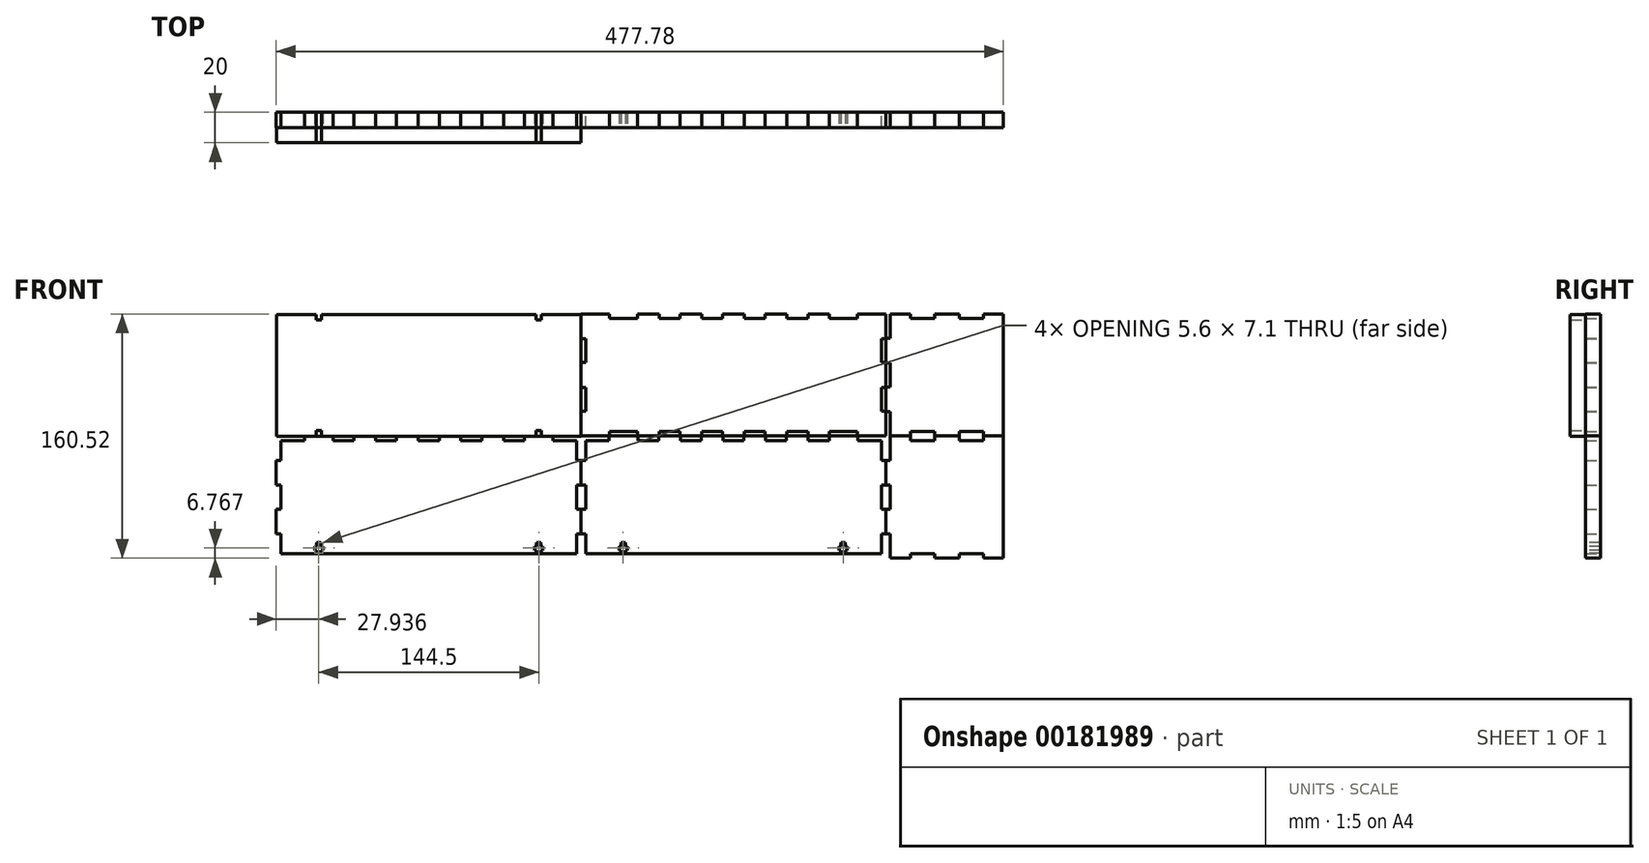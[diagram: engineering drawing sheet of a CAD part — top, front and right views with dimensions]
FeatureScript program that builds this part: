
annotation { "Feature Type Name" : "Feature", "Feature Type Description" : "" }
export const myFeature = defineFeature(function(context is Context, id is Id, definition is map)
    precondition{}
    {
        {
            var Q0;
            Q0=qCreatedBy(makeId("Front.planeOp"),FACE);
            var sketch = newSketch(context, id + "F0", { "sketchPlane" : qUnion([Q0])});
            skLineSegment(sketch, "E0", {"start": v(-38.63, 80.26) * mm, "end": v(-19.87, 80.26) * mm});
            skLineSegment(sketch, "E1", {"start": v(-19.87, 80.26) * mm, "end": v(-19.87, 77.26) * mm});
            skLineSegment(sketch, "E2", {"start": v(-19.87, 77.26) * mm, "end": v(-1.63, 77.26) * mm});
            skLineSegment(sketch, "E3", {"start": v(-1.63, 77.26) * mm, "end": v(-1.63, 80.26) * mm});
            skLineSegment(sketch, "E4", {"start": v(-1.63, 80.26) * mm, "end": v(12.63, 80.26) * mm});
            skLineSegment(sketch, "E5", {"start": v(12.63, 80.26) * mm, "end": v(12.63, 77.26) * mm});
            skLineSegment(sketch, "E6", {"start": v(12.63, 77.26) * mm, "end": v(26.37, 77.26) * mm});
            skLineSegment(sketch, "E7", {"start": v(26.37, 77.26) * mm, "end": v(26.37, 80.26) * mm});
            skLineSegment(sketch, "E8", {"start": v(26.37, 80.26) * mm, "end": v(40.63, 80.26) * mm});
            skLineSegment(sketch, "E9", {"start": v(40.63, 80.26) * mm, "end": v(40.63, 77.26) * mm});
            skLineSegment(sketch, "E10", {"start": v(40.63, 77.26) * mm, "end": v(54.37, 77.26) * mm});
            skLineSegment(sketch, "E11", {"start": v(54.37, 77.26) * mm, "end": v(54.37, 80.26) * mm});
            skLineSegment(sketch, "E12", {"start": v(54.37, 80.26) * mm, "end": v(68.63, 80.26) * mm});
            skLineSegment(sketch, "E13", {"start": v(68.63, 80.26) * mm, "end": v(68.63, 77.26) * mm});
            skLineSegment(sketch, "E14", {"start": v(68.63, 77.26) * mm, "end": v(82.37, 77.26) * mm});
            skLineSegment(sketch, "E15", {"start": v(82.37, 77.26) * mm, "end": v(82.37, 80.26) * mm});
            skLineSegment(sketch, "E16", {"start": v(82.37, 80.26) * mm, "end": v(96.63, 80.26) * mm});
            skLineSegment(sketch, "E17", {"start": v(96.63, 80.26) * mm, "end": v(96.63, 77.26) * mm});
            skLineSegment(sketch, "E18", {"start": v(96.63, 77.26) * mm, "end": v(110.37, 77.26) * mm});
            skLineSegment(sketch, "E19", {"start": v(110.37, 77.26) * mm, "end": v(110.37, 80.26) * mm});
            skLineSegment(sketch, "E20", {"start": v(110.37, 80.26) * mm, "end": v(124.63, 80.26) * mm});
            skLineSegment(sketch, "E21", {"start": v(124.63, 80.26) * mm, "end": v(124.63, 77.26) * mm});
            skLineSegment(sketch, "E22", {"start": v(124.63, 77.26) * mm, "end": v(142.87, 77.26) * mm});
            skLineSegment(sketch, "E23", {"start": v(142.87, 77.26) * mm, "end": v(142.87, 80.26) * mm});
            skLineSegment(sketch, "E24", {"start": v(142.87, 80.26) * mm, "end": v(161.63, 80.26) * mm});
            skLineSegment(sketch, "E25", {"start": v(161.63, 80.26) * mm, "end": v(161.63, 64) * mm});
            skLineSegment(sketch, "E26", {"start": v(161.63, 64) * mm, "end": v(158.63, 64) * mm});
            skLineSegment(sketch, "E27", {"start": v(158.63, 64) * mm, "end": v(158.63, 48.26) * mm});
            skLineSegment(sketch, "E28", {"start": v(158.63, 48.26) * mm, "end": v(161.63, 48.26) * mm});
            skLineSegment(sketch, "E29", {"start": v(161.63, 48.26) * mm, "end": v(161.63, 32) * mm});
            skLineSegment(sketch, "E30", {"start": v(161.63, 32) * mm, "end": v(158.63, 32) * mm});
            skLineSegment(sketch, "E31", {"start": v(158.63, 32) * mm, "end": v(158.63, 16.26) * mm});
            skLineSegment(sketch, "E32", {"start": v(158.63, 16.26) * mm, "end": v(161.63, 16.26) * mm});
            skLineSegment(sketch, "E33", {"start": v(161.63, 16.26) * mm, "end": v(161.63, 0) * mm});
            skLineSegment(sketch, "E34", {"start": v(161.63, 0) * mm, "end": v(142.87, 0) * mm});
            skLineSegment(sketch, "E35", {"start": v(142.87, 0) * mm, "end": v(142.87, 3) * mm});
            skLineSegment(sketch, "E36", {"start": v(142.87, 3) * mm, "end": v(124.63, 3) * mm});
            skLineSegment(sketch, "E37", {"start": v(124.63, 3) * mm, "end": v(124.63, 0) * mm});
            skLineSegment(sketch, "E38", {"start": v(124.63, 0) * mm, "end": v(110.37, 0) * mm});
            skLineSegment(sketch, "E39", {"start": v(110.37, 0) * mm, "end": v(110.37, 3) * mm});
            skLineSegment(sketch, "E40", {"start": v(110.37, 3) * mm, "end": v(96.63, 3) * mm});
            skLineSegment(sketch, "E41", {"start": v(96.63, 3) * mm, "end": v(96.63, 0) * mm});
            skLineSegment(sketch, "E42", {"start": v(96.63, 0) * mm, "end": v(82.37, 0) * mm});
            skLineSegment(sketch, "E43", {"start": v(82.37, 0) * mm, "end": v(82.37, 3) * mm});
            skLineSegment(sketch, "E44", {"start": v(82.37, 3) * mm, "end": v(68.63, 3) * mm});
            skLineSegment(sketch, "E45", {"start": v(68.63, 3) * mm, "end": v(68.63, 0) * mm});
            skLineSegment(sketch, "E46", {"start": v(68.63, 0) * mm, "end": v(54.37, 0) * mm});
            skLineSegment(sketch, "E47", {"start": v(54.37, 0) * mm, "end": v(54.37, 3) * mm});
            skLineSegment(sketch, "E48", {"start": v(54.37, 3) * mm, "end": v(40.63, 3) * mm});
            skLineSegment(sketch, "E49", {"start": v(40.63, 3) * mm, "end": v(40.63, 0) * mm});
            skLineSegment(sketch, "E50", {"start": v(40.63, 0) * mm, "end": v(26.37, 0) * mm});
            skLineSegment(sketch, "E51", {"start": v(26.37, 0) * mm, "end": v(26.37, 3) * mm});
            skLineSegment(sketch, "E52", {"start": v(26.37, 3) * mm, "end": v(12.63, 3) * mm});
            skLineSegment(sketch, "E53", {"start": v(12.63, 3) * mm, "end": v(12.63, 0) * mm});
            skLineSegment(sketch, "E54", {"start": v(12.63, 0) * mm, "end": v(-1.63, 0) * mm});
            skLineSegment(sketch, "E55", {"start": v(-1.63, 0) * mm, "end": v(-1.63, 3) * mm});
            skLineSegment(sketch, "E56", {"start": v(-1.63, 3) * mm, "end": v(-19.87, 3) * mm});
            skLineSegment(sketch, "E57", {"start": v(-19.87, 3) * mm, "end": v(-19.87, 0) * mm});
            skLineSegment(sketch, "E58", {"start": v(-19.87, 0) * mm, "end": v(-38.63, 0) * mm});
            skLineSegment(sketch, "E59", {"start": v(-38.63, 0) * mm, "end": v(-38.63, 16.26) * mm});
            skLineSegment(sketch, "E60", {"start": v(-38.63, 16.26) * mm, "end": v(-35.63, 16.26) * mm});
            skLineSegment(sketch, "E61", {"start": v(-35.63, 16.26) * mm, "end": v(-35.63, 32) * mm});
            skLineSegment(sketch, "E62", {"start": v(-35.63, 32) * mm, "end": v(-38.63, 32) * mm});
            skLineSegment(sketch, "E63", {"start": v(-38.63, 32) * mm, "end": v(-38.63, 48.26) * mm});
            skLineSegment(sketch, "E64", {"start": v(-38.63, 48.26) * mm, "end": v(-35.63, 48.26) * mm});
            skLineSegment(sketch, "E65", {"start": v(-35.63, 48.26) * mm, "end": v(-35.63, 64) * mm});
            skLineSegment(sketch, "E66", {"start": v(-35.63, 64) * mm, "end": v(-38.63, 64) * mm});
            skLineSegment(sketch, "E67", {"start": v(-38.63, 64) * mm, "end": v(-38.63, 80.26) * mm});
            skLineSegment(sketch, "E68", {"start": v(238.89, 0) * mm, "end": v(225.63, 0) * mm});
            skLineSegment(sketch, "E69", {"start": v(225.63, 0) * mm, "end": v(225.63, 3) * mm});
            skLineSegment(sketch, "E70", {"start": v(225.63, 3) * mm, "end": v(209.89, 3) * mm});
            skLineSegment(sketch, "E71", {"start": v(209.89, 3) * mm, "end": v(209.89, 0) * mm});
            skLineSegment(sketch, "E72", {"start": v(209.89, 0) * mm, "end": v(193.63, 0) * mm});
            skLineSegment(sketch, "E73", {"start": v(193.63, 0) * mm, "end": v(193.63, 3) * mm});
            skLineSegment(sketch, "E74", {"start": v(193.63, 3) * mm, "end": v(177.89, 3) * mm});
            skLineSegment(sketch, "E75", {"start": v(177.89, 3) * mm, "end": v(177.89, 0) * mm});
            skLineSegment(sketch, "E76", {"start": v(177.89, 0) * mm, "end": v(164.63, 0) * mm});
            skLineSegment(sketch, "E77", {"start": v(164.63, 0) * mm, "end": v(164.63, 16) * mm});
            skLineSegment(sketch, "E78", {"start": v(164.63, 16) * mm, "end": v(161.63, 16) * mm});
            skLineSegment(sketch, "E79", {"start": v(161.63, 16) * mm, "end": v(161.63, 32.26) * mm});
            skLineSegment(sketch, "E80", {"start": v(161.63, 32.26) * mm, "end": v(164.63, 32.26) * mm});
            skLineSegment(sketch, "E81", {"start": v(164.63, 32.26) * mm, "end": v(164.63, 48) * mm});
            skLineSegment(sketch, "E82", {"start": v(164.63, 48) * mm, "end": v(161.63, 48) * mm});
            skLineSegment(sketch, "E83", {"start": v(161.63, 48) * mm, "end": v(161.63, 64.26) * mm});
            skLineSegment(sketch, "E84", {"start": v(161.63, 64.26) * mm, "end": v(164.63, 64.26) * mm});
            skLineSegment(sketch, "E85", {"start": v(164.63, 64.26) * mm, "end": v(164.63, 80.26) * mm});
            skLineSegment(sketch, "E86", {"start": v(164.63, 80.26) * mm, "end": v(177.89, 80.26) * mm});
            skLineSegment(sketch, "E87", {"start": v(177.89, 80.26) * mm, "end": v(177.89, 77.26) * mm});
            skLineSegment(sketch, "E88", {"start": v(177.89, 77.26) * mm, "end": v(193.63, 77.26) * mm});
            skLineSegment(sketch, "E89", {"start": v(193.63, 77.26) * mm, "end": v(193.63, 80.26) * mm});
            skLineSegment(sketch, "E90", {"start": v(193.63, 80.26) * mm, "end": v(209.89, 80.26) * mm});
            skLineSegment(sketch, "E91", {"start": v(209.89, 80.26) * mm, "end": v(209.89, 77.26) * mm});
            skLineSegment(sketch, "E92", {"start": v(209.89, 77.26) * mm, "end": v(225.63, 77.26) * mm});
            skLineSegment(sketch, "E93", {"start": v(225.63, 77.26) * mm, "end": v(225.63, 80.26) * mm});
            skLineSegment(sketch, "E94", {"start": v(225.63, 80.26) * mm, "end": v(238.89, 80.26) * mm});
            skLineSegment(sketch, "E95", {"start": v(238.89, -80.26) * mm, "end": v(225.63, -80.26) * mm});
            skLineSegment(sketch, "E96", {"start": v(225.63, -80.26) * mm, "end": v(225.63, -77.26) * mm});
            skLineSegment(sketch, "E97", {"start": v(225.63, -77.26) * mm, "end": v(209.89, -77.26) * mm});
            skLineSegment(sketch, "E98", {"start": v(209.89, -77.26) * mm, "end": v(209.89, -80.26) * mm});
            skLineSegment(sketch, "E99", {"start": v(209.89, -80.26) * mm, "end": v(193.63, -80.26) * mm});
            skLineSegment(sketch, "E100", {"start": v(193.63, -80.26) * mm, "end": v(193.63, -77.26) * mm});
            skLineSegment(sketch, "E101", {"start": v(193.63, -77.26) * mm, "end": v(177.89, -77.26) * mm});
            skLineSegment(sketch, "E102", {"start": v(177.89, -77.26) * mm, "end": v(177.89, -80.26) * mm});
            skLineSegment(sketch, "E103", {"start": v(177.89, -80.26) * mm, "end": v(164.63, -80.26) * mm});
            skLineSegment(sketch, "E104", {"start": v(164.63, -80.26) * mm, "end": v(164.63, -64.26) * mm});
            skLineSegment(sketch, "E105", {"start": v(164.63, -64.26) * mm, "end": v(161.63, -64.26) * mm});
            skLineSegment(sketch, "E106", {"start": v(161.63, -64.26) * mm, "end": v(161.63, -48) * mm});
            skLineSegment(sketch, "E107", {"start": v(161.63, -48) * mm, "end": v(164.63, -48) * mm});
            skLineSegment(sketch, "E108", {"start": v(164.63, -48) * mm, "end": v(164.63, -32.26) * mm});
            skLineSegment(sketch, "E109", {"start": v(164.63, -32.26) * mm, "end": v(161.63, -32.26) * mm});
            skLineSegment(sketch, "E110", {"start": v(161.63, -32.26) * mm, "end": v(161.63, -16) * mm});
            skLineSegment(sketch, "E111", {"start": v(161.63, -16) * mm, "end": v(164.63, -16) * mm});
            skLineSegment(sketch, "E112", {"start": v(164.63, -16) * mm, "end": v(164.63, 0) * mm});
            skLineSegment(sketch, "E113", {"start": v(164.63, 0) * mm, "end": v(177.89, 0) * mm});
            skLineSegment(sketch, "E114", {"start": v(177.89, 0) * mm, "end": v(177.89, -3) * mm});
            skLineSegment(sketch, "E115", {"start": v(177.89, -3) * mm, "end": v(193.63, -3) * mm});
            skLineSegment(sketch, "E116", {"start": v(193.63, -3) * mm, "end": v(193.63, 0) * mm});
            skLineSegment(sketch, "E117", {"start": v(193.63, 0) * mm, "end": v(209.89, 0) * mm});
            skLineSegment(sketch, "E118", {"start": v(209.89, 0) * mm, "end": v(209.89, -3) * mm});
            skLineSegment(sketch, "E119", {"start": v(209.89, -3) * mm, "end": v(225.63, -3) * mm});
            skLineSegment(sketch, "E120", {"start": v(225.63, -3) * mm, "end": v(225.63, 0) * mm});
            skLineSegment(sketch, "E121", {"start": v(225.63, 0) * mm, "end": v(238.89, 0) * mm});
            skLineSegment(sketch, "E122", {"start": v(-235.89, -77.26) * mm, "end": v(-235.89, -64.26) * mm});
            skLineSegment(sketch, "E123", {"start": v(-235.89, -64.26) * mm, "end": v(-238.89, -64.26) * mm});
            skLineSegment(sketch, "E124", {"start": v(-238.89, -64.26) * mm, "end": v(-238.89, -48) * mm});
            skLineSegment(sketch, "E125", {"start": v(-238.89, -48) * mm, "end": v(-235.89, -48) * mm});
            skLineSegment(sketch, "E126", {"start": v(-235.89, -48) * mm, "end": v(-235.89, -32.26) * mm});
            skLineSegment(sketch, "E127", {"start": v(-235.89, -32.26) * mm, "end": v(-238.89, -32.26) * mm});
            skLineSegment(sketch, "E128", {"start": v(-238.89, -32.26) * mm, "end": v(-238.89, -16) * mm});
            skLineSegment(sketch, "E129", {"start": v(-238.89, -16) * mm, "end": v(-235.89, -16) * mm});
            skLineSegment(sketch, "E130", {"start": v(-235.89, -16) * mm, "end": v(-235.89, -3) * mm});
            skLineSegment(sketch, "E131", {"start": v(-235.89, -3) * mm, "end": v(-220.39, -3) * mm});
            skLineSegment(sketch, "E132", {"start": v(-220.39, -3) * mm, "end": v(-220.39, 0) * mm});
            skLineSegment(sketch, "E133", {"start": v(-220.39, 0) * mm, "end": v(-201.63, 0) * mm});
            skLineSegment(sketch, "E134", {"start": v(-201.63, 0) * mm, "end": v(-201.63, -3) * mm});
            skLineSegment(sketch, "E135", {"start": v(-201.63, -3) * mm, "end": v(-187.89, -3) * mm});
            skLineSegment(sketch, "E136", {"start": v(-187.89, -3) * mm, "end": v(-187.89, 0) * mm});
            skLineSegment(sketch, "E137", {"start": v(-187.89, 0) * mm, "end": v(-173.63, 0) * mm});
            skLineSegment(sketch, "E138", {"start": v(-173.63, 0) * mm, "end": v(-173.63, -3) * mm});
            skLineSegment(sketch, "E139", {"start": v(-173.63, -3) * mm, "end": v(-159.89, -3) * mm});
            skLineSegment(sketch, "E140", {"start": v(-159.89, -3) * mm, "end": v(-159.89, 0) * mm});
            skLineSegment(sketch, "E141", {"start": v(-159.89, 0) * mm, "end": v(-145.63, 0) * mm});
            skLineSegment(sketch, "E142", {"start": v(-145.63, 0) * mm, "end": v(-145.63, -3) * mm});
            skLineSegment(sketch, "E143", {"start": v(-145.63, -3) * mm, "end": v(-131.89, -3) * mm});
            skLineSegment(sketch, "E144", {"start": v(-131.89, -3) * mm, "end": v(-131.89, 0) * mm});
            skLineSegment(sketch, "E145", {"start": v(-131.89, 0) * mm, "end": v(-117.63, 0) * mm});
            skLineSegment(sketch, "E146", {"start": v(-117.63, 0) * mm, "end": v(-117.63, -3) * mm});
            skLineSegment(sketch, "E147", {"start": v(-117.63, -3) * mm, "end": v(-103.89, -3) * mm});
            skLineSegment(sketch, "E148", {"start": v(-103.89, -3) * mm, "end": v(-103.89, 0) * mm});
            skLineSegment(sketch, "E149", {"start": v(-103.89, 0) * mm, "end": v(-89.63, 0) * mm});
            skLineSegment(sketch, "E150", {"start": v(-89.63, 0) * mm, "end": v(-89.63, -3) * mm});
            skLineSegment(sketch, "E151", {"start": v(-89.63, -3) * mm, "end": v(-75.89, -3) * mm});
            skLineSegment(sketch, "E152", {"start": v(-75.89, -3) * mm, "end": v(-75.89, 0) * mm});
            skLineSegment(sketch, "E153", {"start": v(-75.89, 0) * mm, "end": v(-57.13, 0) * mm});
            skLineSegment(sketch, "E154", {"start": v(-57.13, 0) * mm, "end": v(-57.13, -3) * mm});
            skLineSegment(sketch, "E155", {"start": v(-57.13, -3) * mm, "end": v(-41.63, -3) * mm});
            skLineSegment(sketch, "E156", {"start": v(-41.63, -3) * mm, "end": v(-41.63, -16) * mm});
            skLineSegment(sketch, "E157", {"start": v(-41.63, -16) * mm, "end": v(-38.63, -16) * mm});
            skLineSegment(sketch, "E158", {"start": v(-38.63, -16) * mm, "end": v(-38.63, -32.26) * mm});
            skLineSegment(sketch, "E159", {"start": v(-38.63, -32.26) * mm, "end": v(-41.63, -32.26) * mm});
            skLineSegment(sketch, "E160", {"start": v(-41.63, -32.26) * mm, "end": v(-41.63, -48) * mm});
            skLineSegment(sketch, "E161", {"start": v(-41.63, -48) * mm, "end": v(-38.63, -48) * mm});
            skLineSegment(sketch, "E162", {"start": v(-38.63, -48) * mm, "end": v(-38.63, -64.26) * mm});
            skLineSegment(sketch, "E163", {"start": v(-38.63, -64.26) * mm, "end": v(-41.63, -64.26) * mm});
            skLineSegment(sketch, "E164", {"start": v(-41.63, -64.26) * mm, "end": v(-41.63, -77.26) * mm});
            skLineSegment(sketch, "E165", {"start": v(-35.63, -77.26) * mm, "end": v(-35.63, -64.26) * mm});
            skLineSegment(sketch, "E166", {"start": v(-35.63, -64.26) * mm, "end": v(-38.63, -64.26) * mm});
            skLineSegment(sketch, "E167", {"start": v(-38.63, -64.26) * mm, "end": v(-38.63, -48) * mm});
            skLineSegment(sketch, "E168", {"start": v(-38.63, -48) * mm, "end": v(-35.63, -48) * mm});
            skLineSegment(sketch, "E169", {"start": v(-35.63, -48) * mm, "end": v(-35.63, -32.26) * mm});
            skLineSegment(sketch, "E170", {"start": v(-35.63, -32.26) * mm, "end": v(-38.63, -32.26) * mm});
            skLineSegment(sketch, "E171", {"start": v(-38.63, -32.26) * mm, "end": v(-38.63, -16) * mm});
            skLineSegment(sketch, "E172", {"start": v(-38.63, -16) * mm, "end": v(-35.63, -16) * mm});
            skLineSegment(sketch, "E173", {"start": v(-35.63, -16) * mm, "end": v(-35.63, -3) * mm});
            skLineSegment(sketch, "E174", {"start": v(-35.63, -3) * mm, "end": v(-20.13, -3) * mm});
            skLineSegment(sketch, "E175", {"start": v(-20.13, -3) * mm, "end": v(-20.13, 0) * mm});
            skLineSegment(sketch, "E176", {"start": v(-20.13, 0) * mm, "end": v(-1.37, 0) * mm});
            skLineSegment(sketch, "E177", {"start": v(-1.37, 0) * mm, "end": v(-1.37, -3) * mm});
            skLineSegment(sketch, "E178", {"start": v(-1.37, -3) * mm, "end": v(12.37, -3) * mm});
            skLineSegment(sketch, "E179", {"start": v(12.37, -3) * mm, "end": v(12.37, 0) * mm});
            skLineSegment(sketch, "E180", {"start": v(12.37, 0) * mm, "end": v(26.63, 0) * mm});
            skLineSegment(sketch, "E181", {"start": v(26.63, 0) * mm, "end": v(26.63, -3) * mm});
            skLineSegment(sketch, "E182", {"start": v(26.63, -3) * mm, "end": v(40.37, -3) * mm});
            skLineSegment(sketch, "E183", {"start": v(40.37, -3) * mm, "end": v(40.37, 0) * mm});
            skLineSegment(sketch, "E184", {"start": v(40.37, 0) * mm, "end": v(54.63, 0) * mm});
            skLineSegment(sketch, "E185", {"start": v(54.63, 0) * mm, "end": v(54.63, -3) * mm});
            skLineSegment(sketch, "E186", {"start": v(54.63, -3) * mm, "end": v(68.37, -3) * mm});
            skLineSegment(sketch, "E187", {"start": v(68.37, -3) * mm, "end": v(68.37, 0) * mm});
            skLineSegment(sketch, "E188", {"start": v(68.37, 0) * mm, "end": v(82.63, 0) * mm});
            skLineSegment(sketch, "E189", {"start": v(82.63, 0) * mm, "end": v(82.63, -3) * mm});
            skLineSegment(sketch, "E190", {"start": v(82.63, -3) * mm, "end": v(96.37, -3) * mm});
            skLineSegment(sketch, "E191", {"start": v(96.37, -3) * mm, "end": v(96.37, 0) * mm});
            skLineSegment(sketch, "E192", {"start": v(96.37, 0) * mm, "end": v(110.63, 0) * mm});
            skLineSegment(sketch, "E193", {"start": v(110.63, 0) * mm, "end": v(110.63, -3) * mm});
            skLineSegment(sketch, "E194", {"start": v(110.63, -3) * mm, "end": v(124.37, -3) * mm});
            skLineSegment(sketch, "E195", {"start": v(124.37, -3) * mm, "end": v(124.37, 0) * mm});
            skLineSegment(sketch, "E196", {"start": v(124.37, 0) * mm, "end": v(143.13, 0) * mm});
            skLineSegment(sketch, "E197", {"start": v(143.13, 0) * mm, "end": v(143.13, -3) * mm});
            skLineSegment(sketch, "E198", {"start": v(143.13, -3) * mm, "end": v(158.63, -3) * mm});
            skLineSegment(sketch, "E199", {"start": v(158.63, -3) * mm, "end": v(158.63, -16) * mm});
            skLineSegment(sketch, "E200", {"start": v(158.63, -16) * mm, "end": v(161.63, -16) * mm});
            skLineSegment(sketch, "E201", {"start": v(161.63, -16) * mm, "end": v(161.63, -32.26) * mm});
            skLineSegment(sketch, "E202", {"start": v(161.63, -32.26) * mm, "end": v(158.63, -32.26) * mm});
            skLineSegment(sketch, "E203", {"start": v(158.63, -32.26) * mm, "end": v(158.63, -48) * mm});
            skLineSegment(sketch, "E204", {"start": v(158.63, -48) * mm, "end": v(161.63, -48) * mm});
            skLineSegment(sketch, "E205", {"start": v(161.63, -48) * mm, "end": v(161.63, -64.26) * mm});
            skLineSegment(sketch, "E206", {"start": v(161.63, -64.26) * mm, "end": v(158.63, -64.26) * mm});
            skLineSegment(sketch, "E207", {"start": v(158.63, -64.26) * mm, "end": v(158.63, -77.26) * mm});
            skLineSegment(sketch, "E208", {"start": v(-38.63, 0) * mm, "end": v(-238.89, 0) * mm});
            skLineSegment(sketch, "E209", {"start": v(-238.89, 0) * mm, "end": v(-238.89, 80.26) * mm});
            skLineSegment(sketch, "E210", {"start": v(-238.89, 80.26) * mm, "end": v(-38.63, 80.26) * mm});
            skLineSegment(sketch, "E211", {"start": v(-38.63, 80.26) * mm, "end": v(-38.63, 0) * mm});
            skLineSegment(sketch, "E212", {"start": v(-235.89, -77.26) * mm, "end": v(-41.63, -77.26) * mm});
            skLineSegment(sketch, "E213", {"start": v(-35.63, -77.26) * mm, "end": v(158.63, -77.26) * mm});
            skLineSegment(sketch, "E214", {"start": v(238.89, 80.26) * mm, "end": v(238.89, 0) * mm});
            skLineSegment(sketch, "E215", {"start": v(238.89, 0) * mm, "end": v(238.89, -80.26) * mm});
            skSolve(sketch);
        }
        {
            var Q0;
            Q0=makeQuery(id+"F0.imprint","IMPRINT",FACE,{"disambiguationData":[TD([[makeQuery(id+"F0.imprint","IMPRINT",EDGE,{"derivedFrom":sQuery(id+"F0.wireOp",EDGE,"E165")}),-1.0]])]});
            var Q1;
            Q1=makeQuery(id+"F0.imprint","IMPRINT",FACE,{"disambiguationData":[TD([[makeQuery(id+"F0.imprint","IMPRINT",EDGE,{"derivedFrom":sQuery(id+"F0.wireOp",EDGE,"E69")}),-1.0]])]});
            extrude(context, id + "F1", {"entities" : qUnion([Q0, Q1]), "depth" : 10 * mm});
        }
        {
            var Q0;
            Q0=makeQuery(id+"F0.imprint","IMPRINT",FACE,{"disambiguationData":[TD([[makeQuery(id+"F0.imprint","IMPRINT",EDGE,{"derivedFrom":sQuery(id+"F0.wireOp",EDGE,"E122")}),-1.0]])]});
            var Q1;
            {var subQ21=sQuery(id+"F0.wireOp",EDGE,"E0");Q1=makeQuery(id+"F0.imprint","IMPRINT",FACE,{"disambiguationData":[TD([[makeQuery(id+"F0.imprint","IMPRINT",EDGE,{"derivedFrom":subQ21}),-1.0]])]});}
            var Q2;
            Q2=makeQuery(id+"F0.imprint","IMPRINT",FACE,{"disambiguationData":[TD([[makeQuery(id+"F0.imprint","IMPRINT",EDGE,{"derivedFrom":sQuery(id+"F0.wireOp",EDGE,"E95")}),-1.0]])]});
            var Q3;
            Q3 = qSketchRegion(id + "F3", true);
            extrude(context, id + "F2", {"entities" : qUnion([Q0, Q1, Q2, Q3]), "depth" : 10 * mm});
        }
        {
            var Q0;
            Q0=makeQuery(id+"F2.opExtrude","CAP_FACE",FACE,{"disambiguationData":[OSD([sQuery(id+"F0.wireOp",EDGE,"E0"),sQuery(id+"F0.wireOp",EDGE,"E1"),sQuery(id+"F0.wireOp",EDGE,"E2"),sQuery(id+"F0.wireOp",EDGE,"E3"),sQuery(id+"F0.wireOp",EDGE,"E4"),sQuery(id+"F0.wireOp",EDGE,"E5"),sQuery(id+"F0.wireOp",EDGE,"E6"),sQuery(id+"F0.wireOp",EDGE,"E7"),sQuery(id+"F0.wireOp",EDGE,"E8"),sQuery(id+"F0.wireOp",EDGE,"E9"),sQuery(id+"F0.wireOp",EDGE,"E10"),sQuery(id+"F0.wireOp",EDGE,"E11"),sQuery(id+"F0.wireOp",EDGE,"E12"),sQuery(id+"F0.wireOp",EDGE,"E13"),sQuery(id+"F0.wireOp",EDGE,"E14"),sQuery(id+"F0.wireOp",EDGE,"E15"),sQuery(id+"F0.wireOp",EDGE,"E16"),sQuery(id+"F0.wireOp",EDGE,"E17"),sQuery(id+"F0.wireOp",EDGE,"E18"),sQuery(id+"F0.wireOp",EDGE,"E19"),sQuery(id+"F0.wireOp",EDGE,"E20"),sQuery(id+"F0.wireOp",EDGE,"E21"),sQuery(id+"F0.wireOp",EDGE,"E22"),sQuery(id+"F0.wireOp",EDGE,"E23"),sQuery(id+"F0.wireOp",EDGE,"E24"),sQuery(id+"F0.wireOp",EDGE,"E25"),sQuery(id+"F0.wireOp",EDGE,"E26"),sQuery(id+"F0.wireOp",EDGE,"E27"),sQuery(id+"F0.wireOp",EDGE,"E28"),sQuery(id+"F0.wireOp",EDGE,"E29"),sQuery(id+"F0.wireOp",EDGE,"E30"),sQuery(id+"F0.wireOp",EDGE,"E31"),sQuery(id+"F0.wireOp",EDGE,"E32"),sQuery(id+"F0.wireOp",EDGE,"E33"),sQuery(id+"F0.wireOp",EDGE,"E34"),sQuery(id+"F0.wireOp",EDGE,"E35"),sQuery(id+"F0.wireOp",EDGE,"E36"),sQuery(id+"F0.wireOp",EDGE,"E37"),sQuery(id+"F0.wireOp",EDGE,"E38"),sQuery(id+"F0.wireOp",EDGE,"E39"),sQuery(id+"F0.wireOp",EDGE,"E40"),sQuery(id+"F0.wireOp",EDGE,"E41"),sQuery(id+"F0.wireOp",EDGE,"E42"),sQuery(id+"F0.wireOp",EDGE,"E43"),sQuery(id+"F0.wireOp",EDGE,"E44"),sQuery(id+"F0.wireOp",EDGE,"E45"),sQuery(id+"F0.wireOp",EDGE,"E46"),sQuery(id+"F0.wireOp",EDGE,"E47"),sQuery(id+"F0.wireOp",EDGE,"E48"),sQuery(id+"F0.wireOp",EDGE,"E49"),sQuery(id+"F0.wireOp",EDGE,"E50"),sQuery(id+"F0.wireOp",EDGE,"E51"),sQuery(id+"F0.wireOp",EDGE,"E52"),sQuery(id+"F0.wireOp",EDGE,"E53"),sQuery(id+"F0.wireOp",EDGE,"E54"),sQuery(id+"F0.wireOp",EDGE,"E55"),sQuery(id+"F0.wireOp",EDGE,"E56"),sQuery(id+"F0.wireOp",EDGE,"E57"),sQuery(id+"F0.wireOp",EDGE,"E58"),sQuery(id+"F0.wireOp",EDGE,"E60"),sQuery(id+"F0.wireOp",EDGE,"E61"),sQuery(id+"F0.wireOp",EDGE,"E62"),sQuery(id+"F0.wireOp",EDGE,"E64"),sQuery(id+"F0.wireOp",EDGE,"E65"),sQuery(id+"F0.wireOp",EDGE,"E66"),sQuery(id+"F0.wireOp",EDGE,"E79"),sQuery(id+"F0.wireOp",EDGE,"E83"),sQuery(id+"F0.wireOp",EDGE,"E176"),sQuery(id+"F0.wireOp",EDGE,"E180"),sQuery(id+"F0.wireOp",EDGE,"E184"),sQuery(id+"F0.wireOp",EDGE,"E188"),sQuery(id+"F0.wireOp",EDGE,"E192"),sQuery(id+"F0.wireOp",EDGE,"E196"),sQuery(id+"F0.wireOp",EDGE,"E211")])],"isStart":false});
            var sketch = newSketch(context, id + "F3", { "sketchPlane" : qUnion([Q0])});
            skLineSegment(sketch, "E216", {"start": v(-235.7, -64.04) * mm, "end": v(-238.7, -64.04) * mm});
            skLineSegment(sketch, "E217", {"start": v(-238.7, -64.04) * mm, "end": v(-238.7, -48.04) * mm});
            skLineSegment(sketch, "E218", {"start": v(-238.7, -48.04) * mm, "end": v(-235.7, -48.04) * mm});
            skLineSegment(sketch, "E219", {"start": v(-235.7, -48.04) * mm, "end": v(-235.7, -41.6) * mm});
            skLineSegment(sketch, "E220", {"start": v(-235.7, -41.6) * mm, "end": v(-233.6, -41.6) * mm});
            skLineSegment(sketch, "E221", {"start": v(-233.6, -41.6) * mm, "end": v(-233.6, -42.84) * mm});
            skLineSegment(sketch, "E222", {"start": v(-233.6, -42.84) * mm, "end": v(-231.1, -42.84) * mm});
            skLineSegment(sketch, "E223", {"start": v(-231.1, -42.84) * mm, "end": v(-231.1, -41.6) * mm});
            skLineSegment(sketch, "E224", {"start": v(-231.1, -41.6) * mm, "end": v(-228.6, -41.6) * mm});
            skLineSegment(sketch, "E225", {"start": v(-228.6, -41.6) * mm, "end": v(-228.6, -38.5) * mm});
            skLineSegment(sketch, "E226", {"start": v(-228.6, -38.5) * mm, "end": v(-231.1, -38.5) * mm});
            skLineSegment(sketch, "E227", {"start": v(-231.1, -38.5) * mm, "end": v(-231.1, -37.24) * mm});
            skLineSegment(sketch, "E228", {"start": v(-231.1, -37.24) * mm, "end": v(-233.6, -37.24) * mm});
            skLineSegment(sketch, "E229", {"start": v(-233.6, -37.24) * mm, "end": v(-233.6, -38.5) * mm});
            skLineSegment(sketch, "E230", {"start": v(-233.6, -38.5) * mm, "end": v(-235.7, -38.5) * mm});
            skLineSegment(sketch, "E231", {"start": v(-235.7, -38.5) * mm, "end": v(-235.7, -32.04) * mm});
            skLineSegment(sketch, "E232", {"start": v(-235.7, -32.04) * mm, "end": v(-238.7, -32.04) * mm});
            skLineSegment(sketch, "E233", {"start": v(-238.7, -32.04) * mm, "end": v(-238.7, -16.04) * mm});
            skLineSegment(sketch, "E234", {"start": v(-238.7, -16.04) * mm, "end": v(-235.7, -16.04) * mm});
            skLineSegment(sketch, "E235", {"start": v(-235.7, -16.04) * mm, "end": v(-235.7, -0.04) * mm});
            skLineSegment(sketch, "E236", {"start": v(-235.7, -0.04) * mm, "end": v(-220.2, -0.04) * mm});
            skLineSegment(sketch, "E237", {"start": v(-220.2, -0.04) * mm, "end": v(-220.2, -3.04) * mm});
            skLineSegment(sketch, "E238", {"start": v(-220.2, -3.04) * mm, "end": v(-212.5, -3.04) * mm});
            skLineSegment(sketch, "E239", {"start": v(-212.5, -3.04) * mm, "end": v(-212.5, -5.14) * mm});
            skLineSegment(sketch, "E240", {"start": v(-212.5, -5.14) * mm, "end": v(-213.75, -5.14) * mm});
            skLineSegment(sketch, "E241", {"start": v(-213.75, -5.14) * mm, "end": v(-213.75, -7.64) * mm});
            skLineSegment(sketch, "E242", {"start": v(-213.75, -7.64) * mm, "end": v(-212.5, -7.64) * mm});
            skLineSegment(sketch, "E243", {"start": v(-212.5, -7.64) * mm, "end": v(-212.5, -10.14) * mm});
            skLineSegment(sketch, "E244", {"start": v(-212.5, -10.14) * mm, "end": v(-209.4, -10.14) * mm});
            skLineSegment(sketch, "E245", {"start": v(-209.4, -10.14) * mm, "end": v(-209.4, -7.64) * mm});
            skLineSegment(sketch, "E246", {"start": v(-209.4, -7.64) * mm, "end": v(-208.15, -7.64) * mm});
            skLineSegment(sketch, "E247", {"start": v(-208.15, -7.64) * mm, "end": v(-208.15, -5.14) * mm});
            skLineSegment(sketch, "E248", {"start": v(-208.15, -5.14) * mm, "end": v(-209.4, -5.14) * mm});
            skLineSegment(sketch, "E249", {"start": v(-209.4, -5.14) * mm, "end": v(-209.4, -3.04) * mm});
            skLineSegment(sketch, "E250", {"start": v(-209.4, -3.04) * mm, "end": v(-201.7, -3.04) * mm});
            skLineSegment(sketch, "E251", {"start": v(-201.7, -3.04) * mm, "end": v(-201.7, -0.04) * mm});
            skLineSegment(sketch, "E252", {"start": v(-201.7, -0.04) * mm, "end": v(-187.7, -0.04) * mm});
            skLineSegment(sketch, "E253", {"start": v(-187.7, -0.04) * mm, "end": v(-187.7, -3.04) * mm});
            skLineSegment(sketch, "E254", {"start": v(-187.7, -3.04) * mm, "end": v(-173.7, -3.04) * mm});
            skLineSegment(sketch, "E255", {"start": v(-173.7, -3.04) * mm, "end": v(-173.7, -0.04) * mm});
            skLineSegment(sketch, "E256", {"start": v(-173.7, -0.04) * mm, "end": v(-159.7, -0.04) * mm});
            skLineSegment(sketch, "E257", {"start": v(-159.7, -0.04) * mm, "end": v(-159.7, -3.04) * mm});
            skLineSegment(sketch, "E258", {"start": v(-159.7, -3.04) * mm, "end": v(-145.7, -3.04) * mm});
            skLineSegment(sketch, "E259", {"start": v(-145.7, -3.04) * mm, "end": v(-145.7, -0.04) * mm});
            skLineSegment(sketch, "E260", {"start": v(-145.7, -0.04) * mm, "end": v(-131.7, -0.04) * mm});
            skLineSegment(sketch, "E261", {"start": v(-131.7, -0.04) * mm, "end": v(-131.7, -3.04) * mm});
            skLineSegment(sketch, "E262", {"start": v(-131.7, -3.04) * mm, "end": v(-117.7, -3.04) * mm});
            skLineSegment(sketch, "E263", {"start": v(-117.7, -3.04) * mm, "end": v(-117.7, -0.04) * mm});
            skLineSegment(sketch, "E264", {"start": v(-117.7, -0.04) * mm, "end": v(-103.7, -0.04) * mm});
            skLineSegment(sketch, "E265", {"start": v(-103.7, -0.04) * mm, "end": v(-103.7, -3.04) * mm});
            skLineSegment(sketch, "E266", {"start": v(-103.7, -3.04) * mm, "end": v(-89.7, -3.04) * mm});
            skLineSegment(sketch, "E267", {"start": v(-89.7, -3.04) * mm, "end": v(-89.7, -0.04) * mm});
            skLineSegment(sketch, "E268", {"start": v(-89.7, -0.04) * mm, "end": v(-75.7, -0.04) * mm});
            skLineSegment(sketch, "E269", {"start": v(-75.7, -0.04) * mm, "end": v(-75.7, -3.04) * mm});
            skLineSegment(sketch, "E270", {"start": v(-75.7, -3.04) * mm, "end": v(-68, -3.04) * mm});
            skLineSegment(sketch, "E271", {"start": v(-68, -3.04) * mm, "end": v(-68, -5.14) * mm});
            skLineSegment(sketch, "E272", {"start": v(-68, -5.14) * mm, "end": v(-69.25, -5.14) * mm});
            skLineSegment(sketch, "E273", {"start": v(-69.25, -5.14) * mm, "end": v(-69.25, -7.64) * mm});
            skLineSegment(sketch, "E274", {"start": v(-69.25, -7.64) * mm, "end": v(-68, -7.64) * mm});
            skLineSegment(sketch, "E275", {"start": v(-68, -7.64) * mm, "end": v(-68, -10.14) * mm});
            skLineSegment(sketch, "E276", {"start": v(-68, -10.14) * mm, "end": v(-64.9, -10.14) * mm});
            skLineSegment(sketch, "E277", {"start": v(-64.9, -10.14) * mm, "end": v(-64.9, -7.64) * mm});
            skLineSegment(sketch, "E278", {"start": v(-64.9, -7.64) * mm, "end": v(-63.65, -7.64) * mm});
            skLineSegment(sketch, "E279", {"start": v(-63.65, -7.64) * mm, "end": v(-63.65, -5.14) * mm});
            skLineSegment(sketch, "E280", {"start": v(-63.65, -5.14) * mm, "end": v(-64.9, -5.14) * mm});
            skLineSegment(sketch, "E281", {"start": v(-64.9, -5.14) * mm, "end": v(-64.9, -3.04) * mm});
            skLineSegment(sketch, "E282", {"start": v(-64.9, -3.04) * mm, "end": v(-57.2, -3.04) * mm});
            skLineSegment(sketch, "E283", {"start": v(-57.2, -3.04) * mm, "end": v(-57.2, -0.04) * mm});
            skLineSegment(sketch, "E284", {"start": v(-57.2, -0.04) * mm, "end": v(-41.7, -0.04) * mm});
            skLineSegment(sketch, "E285", {"start": v(-41.7, -0.04) * mm, "end": v(-41.7, -16.04) * mm});
            skLineSegment(sketch, "E286", {"start": v(-41.7, -16.04) * mm, "end": v(-38.7, -16.04) * mm});
            skLineSegment(sketch, "E287", {"start": v(-38.7, -16.04) * mm, "end": v(-38.7, -32.04) * mm});
            skLineSegment(sketch, "E288", {"start": v(-38.7, -32.04) * mm, "end": v(-41.7, -32.04) * mm});
            skLineSegment(sketch, "E289", {"start": v(-41.7, -32.04) * mm, "end": v(-41.7, -38.5) * mm});
            skLineSegment(sketch, "E290", {"start": v(-41.7, -38.5) * mm, "end": v(-43.8, -38.5) * mm});
            skLineSegment(sketch, "E291", {"start": v(-43.8, -38.5) * mm, "end": v(-43.8, -37.24) * mm});
            skLineSegment(sketch, "E292", {"start": v(-43.8, -37.24) * mm, "end": v(-46.3, -37.24) * mm});
            skLineSegment(sketch, "E293", {"start": v(-46.3, -37.24) * mm, "end": v(-46.3, -38.5) * mm});
            skLineSegment(sketch, "E294", {"start": v(-46.3, -38.5) * mm, "end": v(-48.8, -38.5) * mm});
            skLineSegment(sketch, "E295", {"start": v(-48.8, -38.5) * mm, "end": v(-48.8, -41.6) * mm});
            skLineSegment(sketch, "E296", {"start": v(-48.8, -41.6) * mm, "end": v(-46.3, -41.6) * mm});
            skLineSegment(sketch, "E297", {"start": v(-46.3, -41.6) * mm, "end": v(-46.3, -42.84) * mm});
            skLineSegment(sketch, "E298", {"start": v(-46.3, -42.84) * mm, "end": v(-43.8, -42.84) * mm});
            skLineSegment(sketch, "E299", {"start": v(-43.8, -42.84) * mm, "end": v(-43.8, -41.6) * mm});
            skLineSegment(sketch, "E300", {"start": v(-43.8, -41.6) * mm, "end": v(-41.7, -41.6) * mm});
            skLineSegment(sketch, "E301", {"start": v(-41.7, -41.6) * mm, "end": v(-41.7, -48.04) * mm});
            skLineSegment(sketch, "E302", {"start": v(-41.7, -48.04) * mm, "end": v(-38.7, -48.04) * mm});
            skLineSegment(sketch, "E303", {"start": v(-38.7, -48.04) * mm, "end": v(-38.7, -64.04) * mm});
            skLineSegment(sketch, "E304", {"start": v(-38.7, -64.04) * mm, "end": v(-41.7, -64.04) * mm});
            skLineSegment(sketch, "E305", {"start": v(-41.7, -64.04) * mm, "end": v(-41.7, -80.04) * mm});
            skLineSegment(sketch, "E306", {"start": v(-41.7, -80.04) * mm, "end": v(-57.2, -80.04) * mm});
            skLineSegment(sketch, "E307", {"start": v(-57.2, -80.04) * mm, "end": v(-57.2, -77.04) * mm});
            skLineSegment(sketch, "E308", {"start": v(-57.2, -77.04) * mm, "end": v(-64.9, -77.04) * mm});
            skLineSegment(sketch, "E309", {"start": v(-64.9, -77.04) * mm, "end": v(-64.9, -74.94) * mm});
            skLineSegment(sketch, "E310", {"start": v(-64.9, -74.94) * mm, "end": v(-63.65, -74.94) * mm});
            skLineSegment(sketch, "E311", {"start": v(-63.65, -74.94) * mm, "end": v(-63.65, -72.44) * mm});
            skLineSegment(sketch, "E312", {"start": v(-63.65, -72.44) * mm, "end": v(-64.9, -72.44) * mm});
            skLineSegment(sketch, "E313", {"start": v(-64.9, -72.44) * mm, "end": v(-64.9, -69.94) * mm});
            skLineSegment(sketch, "E314", {"start": v(-64.9, -69.94) * mm, "end": v(-68, -69.94) * mm});
            skLineSegment(sketch, "E315", {"start": v(-68, -69.94) * mm, "end": v(-68, -72.44) * mm});
            skLineSegment(sketch, "E316", {"start": v(-68, -72.44) * mm, "end": v(-69.25, -72.44) * mm});
            skLineSegment(sketch, "E317", {"start": v(-69.25, -72.44) * mm, "end": v(-69.25, -74.94) * mm});
            skLineSegment(sketch, "E318", {"start": v(-69.25, -74.94) * mm, "end": v(-68, -74.94) * mm});
            skLineSegment(sketch, "E319", {"start": v(-68, -74.94) * mm, "end": v(-68, -77.04) * mm});
            skLineSegment(sketch, "E320", {"start": v(-68, -77.04) * mm, "end": v(-75.7, -77.04) * mm});
            skLineSegment(sketch, "E321", {"start": v(-75.7, -77.04) * mm, "end": v(-75.7, -80.04) * mm});
            skLineSegment(sketch, "E322", {"start": v(-75.7, -80.04) * mm, "end": v(-89.7, -80.04) * mm});
            skLineSegment(sketch, "E323", {"start": v(-89.7, -80.04) * mm, "end": v(-89.7, -77.04) * mm});
            skLineSegment(sketch, "E324", {"start": v(-89.7, -77.04) * mm, "end": v(-103.7, -77.04) * mm});
            skLineSegment(sketch, "E325", {"start": v(-103.7, -77.04) * mm, "end": v(-103.7, -80.04) * mm});
            skLineSegment(sketch, "E326", {"start": v(-103.7, -80.04) * mm, "end": v(-117.7, -80.04) * mm});
            skLineSegment(sketch, "E327", {"start": v(-117.7, -80.04) * mm, "end": v(-117.7, -77.04) * mm});
            skLineSegment(sketch, "E328", {"start": v(-117.7, -77.04) * mm, "end": v(-131.7, -77.04) * mm});
            skLineSegment(sketch, "E329", {"start": v(-131.7, -77.04) * mm, "end": v(-131.7, -80.04) * mm});
            skLineSegment(sketch, "E330", {"start": v(-131.7, -80.04) * mm, "end": v(-145.7, -80.04) * mm});
            skLineSegment(sketch, "E331", {"start": v(-145.7, -80.04) * mm, "end": v(-145.7, -77.04) * mm});
            skLineSegment(sketch, "E332", {"start": v(-145.7, -77.04) * mm, "end": v(-159.7, -77.04) * mm});
            skLineSegment(sketch, "E333", {"start": v(-159.7, -77.04) * mm, "end": v(-159.7, -80.04) * mm});
            skLineSegment(sketch, "E334", {"start": v(-159.7, -80.04) * mm, "end": v(-173.7, -80.04) * mm});
            skLineSegment(sketch, "E335", {"start": v(-173.7, -80.04) * mm, "end": v(-173.7, -77.04) * mm});
            skLineSegment(sketch, "E336", {"start": v(-173.7, -77.04) * mm, "end": v(-187.7, -77.04) * mm});
            skLineSegment(sketch, "E337", {"start": v(-187.7, -77.04) * mm, "end": v(-187.7, -80.04) * mm});
            skLineSegment(sketch, "E338", {"start": v(-187.7, -80.04) * mm, "end": v(-201.7, -80.04) * mm});
            skLineSegment(sketch, "E339", {"start": v(-201.7, -80.04) * mm, "end": v(-201.7, -77.04) * mm});
            skLineSegment(sketch, "E340", {"start": v(-201.7, -77.04) * mm, "end": v(-209.4, -77.04) * mm});
            skLineSegment(sketch, "E341", {"start": v(-209.4, -77.04) * mm, "end": v(-209.4, -74.94) * mm});
            skLineSegment(sketch, "E342", {"start": v(-209.4, -74.94) * mm, "end": v(-208.15, -74.94) * mm});
            skLineSegment(sketch, "E343", {"start": v(-208.15, -74.94) * mm, "end": v(-208.15, -72.44) * mm});
            skLineSegment(sketch, "E344", {"start": v(-208.15, -72.44) * mm, "end": v(-209.4, -72.44) * mm});
            skLineSegment(sketch, "E345", {"start": v(-209.4, -72.44) * mm, "end": v(-209.4, -69.94) * mm});
            skLineSegment(sketch, "E346", {"start": v(-209.4, -69.94) * mm, "end": v(-212.5, -69.94) * mm});
            skLineSegment(sketch, "E347", {"start": v(-212.5, -69.94) * mm, "end": v(-212.5, -72.44) * mm});
            skLineSegment(sketch, "E348", {"start": v(-212.5, -72.44) * mm, "end": v(-213.75, -72.44) * mm});
            skLineSegment(sketch, "E349", {"start": v(-213.75, -72.44) * mm, "end": v(-213.75, -74.94) * mm});
            skLineSegment(sketch, "E350", {"start": v(-213.75, -74.94) * mm, "end": v(-212.5, -74.94) * mm});
            skLineSegment(sketch, "E351", {"start": v(-212.5, -74.94) * mm, "end": v(-212.5, -77.04) * mm});
            skLineSegment(sketch, "E352", {"start": v(-212.5, -77.04) * mm, "end": v(-220.2, -77.04) * mm});
            skLineSegment(sketch, "E353", {"start": v(-220.2, -77.04) * mm, "end": v(-220.2, -80.04) * mm});
            skLineSegment(sketch, "E354", {"start": v(-220.2, -80.04) * mm, "end": v(-235.7, -80.04) * mm});
            skLineSegment(sketch, "E355", {"start": v(-235.7, -80.04) * mm, "end": v(-235.7, -64.04) * mm});
            skLineSegment(sketch, "E356", {"start": v(-35.7, -64.04) * mm, "end": v(-38.7, -64.04) * mm});
            skLineSegment(sketch, "E357", {"start": v(-38.7, -64.04) * mm, "end": v(-38.7, -48.04) * mm});
            skLineSegment(sketch, "E358", {"start": v(-38.7, -48.04) * mm, "end": v(-35.7, -48.04) * mm});
            skLineSegment(sketch, "E359", {"start": v(-35.7, -48.04) * mm, "end": v(-35.7, -41.6) * mm});
            skLineSegment(sketch, "E360", {"start": v(-35.7, -41.6) * mm, "end": v(-33.6, -41.6) * mm});
            skLineSegment(sketch, "E361", {"start": v(-33.6, -41.6) * mm, "end": v(-33.6, -42.84) * mm});
            skLineSegment(sketch, "E362", {"start": v(-33.6, -42.84) * mm, "end": v(-31.1, -42.84) * mm});
            skLineSegment(sketch, "E363", {"start": v(-31.1, -42.84) * mm, "end": v(-31.1, -41.6) * mm});
            skLineSegment(sketch, "E364", {"start": v(-31.1, -41.6) * mm, "end": v(-28.6, -41.6) * mm});
            skLineSegment(sketch, "E365", {"start": v(-28.6, -41.6) * mm, "end": v(-28.6, -38.5) * mm});
            skLineSegment(sketch, "E366", {"start": v(-28.6, -38.5) * mm, "end": v(-31.1, -38.5) * mm});
            skLineSegment(sketch, "E367", {"start": v(-31.1, -38.5) * mm, "end": v(-31.1, -37.24) * mm});
            skLineSegment(sketch, "E368", {"start": v(-31.1, -37.24) * mm, "end": v(-33.6, -37.24) * mm});
            skLineSegment(sketch, "E369", {"start": v(-33.6, -37.24) * mm, "end": v(-33.6, -38.5) * mm});
            skLineSegment(sketch, "E370", {"start": v(-33.6, -38.5) * mm, "end": v(-35.7, -38.5) * mm});
            skLineSegment(sketch, "E371", {"start": v(-35.7, -38.5) * mm, "end": v(-35.7, -32.04) * mm});
            skLineSegment(sketch, "E372", {"start": v(-35.7, -32.04) * mm, "end": v(-38.7, -32.04) * mm});
            skLineSegment(sketch, "E373", {"start": v(-38.7, -32.04) * mm, "end": v(-38.7, -16.04) * mm});
            skLineSegment(sketch, "E374", {"start": v(-38.7, -16.04) * mm, "end": v(-35.7, -16.04) * mm});
            skLineSegment(sketch, "E375", {"start": v(-35.7, -16.04) * mm, "end": v(-35.7, -0.04) * mm});
            skLineSegment(sketch, "E376", {"start": v(-35.7, -0.04) * mm, "end": v(-20.2, -0.04) * mm});
            skLineSegment(sketch, "E377", {"start": v(-20.2, -0.04) * mm, "end": v(-20.2, -3.04) * mm});
            skLineSegment(sketch, "E378", {"start": v(-20.2, -3.04) * mm, "end": v(-12.5, -3.04) * mm});
            skLineSegment(sketch, "E379", {"start": v(-12.5, -3.04) * mm, "end": v(-12.5, -5.14) * mm});
            skLineSegment(sketch, "E380", {"start": v(-12.5, -5.14) * mm, "end": v(-13.75, -5.14) * mm});
            skLineSegment(sketch, "E381", {"start": v(-13.75, -5.14) * mm, "end": v(-13.75, -7.64) * mm});
            skLineSegment(sketch, "E382", {"start": v(-13.75, -7.64) * mm, "end": v(-12.5, -7.64) * mm});
            skLineSegment(sketch, "E383", {"start": v(-12.5, -7.64) * mm, "end": v(-12.5, -10.14) * mm});
            skLineSegment(sketch, "E384", {"start": v(-12.5, -10.14) * mm, "end": v(-9.4, -10.14) * mm});
            skLineSegment(sketch, "E385", {"start": v(-9.4, -10.14) * mm, "end": v(-9.4, -7.64) * mm});
            skLineSegment(sketch, "E386", {"start": v(-9.4, -7.64) * mm, "end": v(-8.15, -7.64) * mm});
            skLineSegment(sketch, "E387", {"start": v(-8.15, -7.64) * mm, "end": v(-8.15, -5.14) * mm});
            skLineSegment(sketch, "E388", {"start": v(-8.15, -5.14) * mm, "end": v(-9.4, -5.14) * mm});
            skLineSegment(sketch, "E389", {"start": v(-9.4, -5.14) * mm, "end": v(-9.4, -3.04) * mm});
            skLineSegment(sketch, "E390", {"start": v(-9.4, -3.04) * mm, "end": v(-1.7, -3.04) * mm});
            skLineSegment(sketch, "E391", {"start": v(-1.7, -3.04) * mm, "end": v(-1.7, -0.04) * mm});
            skLineSegment(sketch, "E392", {"start": v(-1.7, -0.04) * mm, "end": v(12.3, -0.04) * mm});
            skLineSegment(sketch, "E393", {"start": v(12.3, -0.04) * mm, "end": v(12.3, -3.04) * mm});
            skLineSegment(sketch, "E394", {"start": v(12.3, -3.04) * mm, "end": v(26.3, -3.04) * mm});
            skLineSegment(sketch, "E395", {"start": v(26.3, -3.04) * mm, "end": v(26.3, -0.04) * mm});
            skLineSegment(sketch, "E396", {"start": v(26.3, -0.04) * mm, "end": v(40.3, -0.04) * mm});
            skLineSegment(sketch, "E397", {"start": v(40.3, -0.04) * mm, "end": v(40.3, -3.04) * mm});
            skLineSegment(sketch, "E398", {"start": v(40.3, -3.04) * mm, "end": v(54.3, -3.04) * mm});
            skLineSegment(sketch, "E399", {"start": v(54.3, -3.04) * mm, "end": v(54.3, -0.04) * mm});
            skLineSegment(sketch, "E400", {"start": v(54.3, -0.04) * mm, "end": v(68.3, -0.04) * mm});
            skLineSegment(sketch, "E401", {"start": v(68.3, -0.04) * mm, "end": v(68.3, -3.04) * mm});
            skLineSegment(sketch, "E402", {"start": v(68.3, -3.04) * mm, "end": v(82.3, -3.04) * mm});
            skLineSegment(sketch, "E403", {"start": v(82.3, -3.04) * mm, "end": v(82.3, -0.04) * mm});
            skLineSegment(sketch, "E404", {"start": v(82.3, -0.04) * mm, "end": v(96.3, -0.04) * mm});
            skLineSegment(sketch, "E405", {"start": v(96.3, -0.04) * mm, "end": v(96.3, -3.04) * mm});
            skLineSegment(sketch, "E406", {"start": v(96.3, -3.04) * mm, "end": v(110.3, -3.04) * mm});
            skLineSegment(sketch, "E407", {"start": v(110.3, -3.04) * mm, "end": v(110.3, -0.04) * mm});
            skLineSegment(sketch, "E408", {"start": v(110.3, -0.04) * mm, "end": v(124.3, -0.04) * mm});
            skLineSegment(sketch, "E409", {"start": v(124.3, -0.04) * mm, "end": v(124.3, -3.04) * mm});
            skLineSegment(sketch, "E410", {"start": v(124.3, -3.04) * mm, "end": v(132, -3.04) * mm});
            skLineSegment(sketch, "E411", {"start": v(132, -3.04) * mm, "end": v(132, -5.14) * mm});
            skLineSegment(sketch, "E412", {"start": v(132, -5.14) * mm, "end": v(130.75, -5.14) * mm});
            skLineSegment(sketch, "E413", {"start": v(130.75, -5.14) * mm, "end": v(130.75, -7.64) * mm});
            skLineSegment(sketch, "E414", {"start": v(130.75, -7.64) * mm, "end": v(132, -7.64) * mm});
            skLineSegment(sketch, "E415", {"start": v(132, -7.64) * mm, "end": v(132, -10.14) * mm});
            skLineSegment(sketch, "E416", {"start": v(132, -10.14) * mm, "end": v(135.1, -10.14) * mm});
            skLineSegment(sketch, "E417", {"start": v(135.1, -10.14) * mm, "end": v(135.1, -7.64) * mm});
            skLineSegment(sketch, "E418", {"start": v(135.1, -7.64) * mm, "end": v(136.35, -7.64) * mm});
            skLineSegment(sketch, "E419", {"start": v(136.35, -7.64) * mm, "end": v(136.35, -5.14) * mm});
            skLineSegment(sketch, "E420", {"start": v(136.35, -5.14) * mm, "end": v(135.1, -5.14) * mm});
            skLineSegment(sketch, "E421", {"start": v(135.1, -5.14) * mm, "end": v(135.1, -3.04) * mm});
            skLineSegment(sketch, "E422", {"start": v(135.1, -3.04) * mm, "end": v(142.8, -3.04) * mm});
            skLineSegment(sketch, "E423", {"start": v(142.8, -3.04) * mm, "end": v(142.8, -0.04) * mm});
            skLineSegment(sketch, "E424", {"start": v(142.8, -0.04) * mm, "end": v(158.3, -0.04) * mm});
            skLineSegment(sketch, "E425", {"start": v(158.3, -0.04) * mm, "end": v(158.3, -16.04) * mm});
            skLineSegment(sketch, "E426", {"start": v(158.3, -16.04) * mm, "end": v(161.3, -16.04) * mm});
            skLineSegment(sketch, "E427", {"start": v(161.3, -16.04) * mm, "end": v(161.3, -32.04) * mm});
            skLineSegment(sketch, "E428", {"start": v(161.3, -32.04) * mm, "end": v(158.3, -32.04) * mm});
            skLineSegment(sketch, "E429", {"start": v(158.3, -32.04) * mm, "end": v(158.3, -38.5) * mm});
            skLineSegment(sketch, "E430", {"start": v(158.3, -38.5) * mm, "end": v(156.2, -38.5) * mm});
            skLineSegment(sketch, "E431", {"start": v(156.2, -38.5) * mm, "end": v(156.2, -37.24) * mm});
            skLineSegment(sketch, "E432", {"start": v(156.2, -37.24) * mm, "end": v(153.7, -37.24) * mm});
            skLineSegment(sketch, "E433", {"start": v(153.7, -37.24) * mm, "end": v(153.7, -38.5) * mm});
            skLineSegment(sketch, "E434", {"start": v(153.7, -38.5) * mm, "end": v(151.2, -38.5) * mm});
            skLineSegment(sketch, "E435", {"start": v(151.2, -38.5) * mm, "end": v(151.2, -41.6) * mm});
            skLineSegment(sketch, "E436", {"start": v(151.2, -41.6) * mm, "end": v(153.7, -41.6) * mm});
            skLineSegment(sketch, "E437", {"start": v(153.7, -41.6) * mm, "end": v(153.7, -42.84) * mm});
            skLineSegment(sketch, "E438", {"start": v(153.7, -42.84) * mm, "end": v(156.2, -42.84) * mm});
            skLineSegment(sketch, "E439", {"start": v(156.2, -42.84) * mm, "end": v(156.2, -41.6) * mm});
            skLineSegment(sketch, "E440", {"start": v(156.2, -41.6) * mm, "end": v(158.3, -41.6) * mm});
            skLineSegment(sketch, "E441", {"start": v(158.3, -41.6) * mm, "end": v(158.3, -48.04) * mm});
            skLineSegment(sketch, "E442", {"start": v(158.3, -48.04) * mm, "end": v(161.3, -48.04) * mm});
            skLineSegment(sketch, "E443", {"start": v(161.3, -48.04) * mm, "end": v(161.3, -64.04) * mm});
            skLineSegment(sketch, "E444", {"start": v(161.3, -64.04) * mm, "end": v(158.3, -64.04) * mm});
            skLineSegment(sketch, "E445", {"start": v(158.3, -64.04) * mm, "end": v(158.3, -80.04) * mm});
            skLineSegment(sketch, "E446", {"start": v(158.3, -80.04) * mm, "end": v(142.8, -80.04) * mm});
            skLineSegment(sketch, "E447", {"start": v(142.8, -80.04) * mm, "end": v(142.8, -77.04) * mm});
            skLineSegment(sketch, "E448", {"start": v(142.8, -77.04) * mm, "end": v(135.1, -77.04) * mm});
            skLineSegment(sketch, "E449", {"start": v(135.1, -77.04) * mm, "end": v(135.1, -74.94) * mm});
            skLineSegment(sketch, "E450", {"start": v(135.1, -74.94) * mm, "end": v(136.35, -74.94) * mm});
            skLineSegment(sketch, "E451", {"start": v(136.35, -74.94) * mm, "end": v(136.35, -72.44) * mm});
            skLineSegment(sketch, "E452", {"start": v(136.35, -72.44) * mm, "end": v(135.1, -72.44) * mm});
            skLineSegment(sketch, "E453", {"start": v(135.1, -72.44) * mm, "end": v(135.1, -69.94) * mm});
            skLineSegment(sketch, "E454", {"start": v(135.1, -69.94) * mm, "end": v(132, -69.94) * mm});
            skLineSegment(sketch, "E455", {"start": v(132, -69.94) * mm, "end": v(132, -72.44) * mm});
            skLineSegment(sketch, "E456", {"start": v(132, -72.44) * mm, "end": v(130.75, -72.44) * mm});
            skLineSegment(sketch, "E457", {"start": v(130.75, -72.44) * mm, "end": v(130.75, -74.94) * mm});
            skLineSegment(sketch, "E458", {"start": v(130.75, -74.94) * mm, "end": v(132, -74.94) * mm});
            skLineSegment(sketch, "E459", {"start": v(132, -74.94) * mm, "end": v(132, -77.04) * mm});
            skLineSegment(sketch, "E460", {"start": v(132, -77.04) * mm, "end": v(124.3, -77.04) * mm});
            skLineSegment(sketch, "E461", {"start": v(124.3, -77.04) * mm, "end": v(124.3, -80.04) * mm});
            skLineSegment(sketch, "E462", {"start": v(124.3, -80.04) * mm, "end": v(110.3, -80.04) * mm});
            skLineSegment(sketch, "E463", {"start": v(110.3, -80.04) * mm, "end": v(110.3, -77.04) * mm});
            skLineSegment(sketch, "E464", {"start": v(110.3, -77.04) * mm, "end": v(96.3, -77.04) * mm});
            skLineSegment(sketch, "E465", {"start": v(96.3, -77.04) * mm, "end": v(96.3, -80.04) * mm});
            skLineSegment(sketch, "E466", {"start": v(96.3, -80.04) * mm, "end": v(82.3, -80.04) * mm});
            skLineSegment(sketch, "E467", {"start": v(82.3, -80.04) * mm, "end": v(82.3, -77.04) * mm});
            skLineSegment(sketch, "E468", {"start": v(82.3, -77.04) * mm, "end": v(68.3, -77.04) * mm});
            skLineSegment(sketch, "E469", {"start": v(68.3, -77.04) * mm, "end": v(68.3, -80.04) * mm});
            skLineSegment(sketch, "E470", {"start": v(68.3, -80.04) * mm, "end": v(54.3, -80.04) * mm});
            skLineSegment(sketch, "E471", {"start": v(54.3, -80.04) * mm, "end": v(54.3, -77.04) * mm});
            skLineSegment(sketch, "E472", {"start": v(54.3, -77.04) * mm, "end": v(40.3, -77.04) * mm});
            skLineSegment(sketch, "E473", {"start": v(40.3, -77.04) * mm, "end": v(40.3, -80.04) * mm});
            skLineSegment(sketch, "E474", {"start": v(40.3, -80.04) * mm, "end": v(26.3, -80.04) * mm});
            skLineSegment(sketch, "E475", {"start": v(26.3, -80.04) * mm, "end": v(26.3, -77.04) * mm});
            skLineSegment(sketch, "E476", {"start": v(26.3, -77.04) * mm, "end": v(12.3, -77.04) * mm});
            skLineSegment(sketch, "E477", {"start": v(12.3, -77.04) * mm, "end": v(12.3, -80.04) * mm});
            skLineSegment(sketch, "E478", {"start": v(12.3, -80.04) * mm, "end": v(-1.7, -80.04) * mm});
            skLineSegment(sketch, "E479", {"start": v(-1.7, -80.04) * mm, "end": v(-1.7, -77.04) * mm});
            skLineSegment(sketch, "E480", {"start": v(-1.7, -77.04) * mm, "end": v(-9.4, -77.04) * mm});
            skLineSegment(sketch, "E481", {"start": v(-9.4, -77.04) * mm, "end": v(-9.4, -74.94) * mm});
            skLineSegment(sketch, "E482", {"start": v(-9.4, -74.94) * mm, "end": v(-8.15, -74.94) * mm});
            skLineSegment(sketch, "E483", {"start": v(-8.15, -74.94) * mm, "end": v(-8.15, -72.44) * mm});
            skLineSegment(sketch, "E484", {"start": v(-8.15, -72.44) * mm, "end": v(-9.4, -72.44) * mm});
            skLineSegment(sketch, "E485", {"start": v(-9.4, -72.44) * mm, "end": v(-9.4, -69.94) * mm});
            skLineSegment(sketch, "E486", {"start": v(-9.4, -69.94) * mm, "end": v(-12.5, -69.94) * mm});
            skLineSegment(sketch, "E487", {"start": v(-12.5, -69.94) * mm, "end": v(-12.5, -72.44) * mm});
            skLineSegment(sketch, "E488", {"start": v(-12.5, -72.44) * mm, "end": v(-13.75, -72.44) * mm});
            skLineSegment(sketch, "E489", {"start": v(-13.75, -72.44) * mm, "end": v(-13.75, -74.94) * mm});
            skLineSegment(sketch, "E490", {"start": v(-13.75, -74.94) * mm, "end": v(-12.5, -74.94) * mm});
            skLineSegment(sketch, "E491", {"start": v(-12.5, -74.94) * mm, "end": v(-12.5, -77.04) * mm});
            skLineSegment(sketch, "E492", {"start": v(-12.5, -77.04) * mm, "end": v(-20.2, -77.04) * mm});
            skLineSegment(sketch, "E493", {"start": v(-20.2, -77.04) * mm, "end": v(-20.2, -80.04) * mm});
            skLineSegment(sketch, "E494", {"start": v(-20.2, -80.04) * mm, "end": v(-35.7, -80.04) * mm});
            skLineSegment(sketch, "E495", {"start": v(-35.7, -80.04) * mm, "end": v(-35.7, -64.04) * mm});
            skLineSegment(sketch, "E496", {"start": v(161.3, -64.04) * mm, "end": v(164.3, -64.04) * mm});
            skLineSegment(sketch, "E497", {"start": v(164.3, -64.04) * mm, "end": v(164.3, -48.04) * mm});
            skLineSegment(sketch, "E498", {"start": v(164.3, -48.04) * mm, "end": v(161.3, -48.04) * mm});
            skLineSegment(sketch, "E499", {"start": v(161.3, -48.04) * mm, "end": v(161.3, -41.9) * mm});
            skLineSegment(sketch, "E500", {"start": v(161.3, -41.9) * mm, "end": v(165, -41.9) * mm});
            skLineSegment(sketch, "E501", {"start": v(165, -41.9) * mm, "end": v(165, -38.2) * mm});
            skLineSegment(sketch, "E502", {"start": v(165, -38.2) * mm, "end": v(161.3, -38.2) * mm});
            skLineSegment(sketch, "E503", {"start": v(161.3, -38.2) * mm, "end": v(161.3, -32.04) * mm});
            skLineSegment(sketch, "E504", {"start": v(161.3, -32.04) * mm, "end": v(164.3, -32.04) * mm});
            skLineSegment(sketch, "E505", {"start": v(164.3, -32.04) * mm, "end": v(164.3, -16.04) * mm});
            skLineSegment(sketch, "E506", {"start": v(164.3, -16.04) * mm, "end": v(161.3, -16.04) * mm});
            skLineSegment(sketch, "E507", {"start": v(161.3, -16.04) * mm, "end": v(161.3, -3.04) * mm});
            skLineSegment(sketch, "E508", {"start": v(161.3, -3.04) * mm, "end": v(177.3, -3.04) * mm});
            skLineSegment(sketch, "E509", {"start": v(177.3, -3.04) * mm, "end": v(177.3, -0.04) * mm});
            skLineSegment(sketch, "E510", {"start": v(177.3, -0.04) * mm, "end": v(193.3, -0.04) * mm});
            skLineSegment(sketch, "E511", {"start": v(193.3, -0.04) * mm, "end": v(193.3, -3.04) * mm});
            skLineSegment(sketch, "E512", {"start": v(193.3, -3.04) * mm, "end": v(199.75, -3.04) * mm});
            skLineSegment(sketch, "E513", {"start": v(199.75, -3.04) * mm, "end": v(199.75, -5.14) * mm});
            skLineSegment(sketch, "E514", {"start": v(199.75, -5.14) * mm, "end": v(198.5, -5.14) * mm});
            skLineSegment(sketch, "E515", {"start": v(198.5, -5.14) * mm, "end": v(198.5, -7.64) * mm});
            skLineSegment(sketch, "E516", {"start": v(198.5, -7.64) * mm, "end": v(199.75, -7.64) * mm});
            skLineSegment(sketch, "E517", {"start": v(199.75, -7.64) * mm, "end": v(199.75, -10.14) * mm});
            skLineSegment(sketch, "E518", {"start": v(199.75, -10.14) * mm, "end": v(202.85, -10.14) * mm});
            skLineSegment(sketch, "E519", {"start": v(202.85, -10.14) * mm, "end": v(202.85, -7.64) * mm});
            skLineSegment(sketch, "E520", {"start": v(202.85, -7.64) * mm, "end": v(204.1, -7.64) * mm});
            skLineSegment(sketch, "E521", {"start": v(204.1, -7.64) * mm, "end": v(204.1, -5.14) * mm});
            skLineSegment(sketch, "E522", {"start": v(204.1, -5.14) * mm, "end": v(202.85, -5.14) * mm});
            skLineSegment(sketch, "E523", {"start": v(202.85, -5.14) * mm, "end": v(202.85, -3.04) * mm});
            skLineSegment(sketch, "E524", {"start": v(202.85, -3.04) * mm, "end": v(209.3, -3.04) * mm});
            skLineSegment(sketch, "E525", {"start": v(209.3, -3.04) * mm, "end": v(209.3, -0.04) * mm});
            skLineSegment(sketch, "E526", {"start": v(209.3, -0.04) * mm, "end": v(225.3, -0.04) * mm});
            skLineSegment(sketch, "E527", {"start": v(225.3, -0.04) * mm, "end": v(225.3, -3.04) * mm});
            skLineSegment(sketch, "E528", {"start": v(225.3, -3.04) * mm, "end": v(241.3, -3.04) * mm});
            skLineSegment(sketch, "E529", {"start": v(241.3, -3.04) * mm, "end": v(241.3, -16.04) * mm});
            skLineSegment(sketch, "E530", {"start": v(241.3, -16.04) * mm, "end": v(238.3, -16.04) * mm});
            skLineSegment(sketch, "E531", {"start": v(238.3, -16.04) * mm, "end": v(238.3, -32.04) * mm});
            skLineSegment(sketch, "E532", {"start": v(238.3, -32.04) * mm, "end": v(241.3, -32.04) * mm});
            skLineSegment(sketch, "E533", {"start": v(241.3, -32.04) * mm, "end": v(241.3, -38.2) * mm});
            skLineSegment(sketch, "E534", {"start": v(241.3, -38.2) * mm, "end": v(237.6, -38.2) * mm});
            skLineSegment(sketch, "E535", {"start": v(237.6, -38.2) * mm, "end": v(237.6, -41.9) * mm});
            skLineSegment(sketch, "E536", {"start": v(237.6, -41.9) * mm, "end": v(241.3, -41.9) * mm});
            skLineSegment(sketch, "E537", {"start": v(241.3, -41.9) * mm, "end": v(241.3, -48.04) * mm});
            skLineSegment(sketch, "E538", {"start": v(241.3, -48.04) * mm, "end": v(238.3, -48.04) * mm});
            skLineSegment(sketch, "E539", {"start": v(238.3, -48.04) * mm, "end": v(238.3, -64.04) * mm});
            skLineSegment(sketch, "E540", {"start": v(238.3, -64.04) * mm, "end": v(241.3, -64.04) * mm});
            skLineSegment(sketch, "E541", {"start": v(241.3, -64.04) * mm, "end": v(241.3, -77.04) * mm});
            skLineSegment(sketch, "E542", {"start": v(241.3, -77.04) * mm, "end": v(225.3, -77.04) * mm});
            skLineSegment(sketch, "E543", {"start": v(225.3, -77.04) * mm, "end": v(225.3, -80.04) * mm});
            skLineSegment(sketch, "E544", {"start": v(225.3, -80.04) * mm, "end": v(209.3, -80.04) * mm});
            skLineSegment(sketch, "E545", {"start": v(209.3, -80.04) * mm, "end": v(209.3, -77.04) * mm});
            skLineSegment(sketch, "E546", {"start": v(209.3, -77.04) * mm, "end": v(202.85, -77.04) * mm});
            skLineSegment(sketch, "E547", {"start": v(202.85, -77.04) * mm, "end": v(202.85, -74.94) * mm});
            skLineSegment(sketch, "E548", {"start": v(202.85, -74.94) * mm, "end": v(204.1, -74.94) * mm});
            skLineSegment(sketch, "E549", {"start": v(204.1, -74.94) * mm, "end": v(204.1, -72.44) * mm});
            skLineSegment(sketch, "E550", {"start": v(204.1, -72.44) * mm, "end": v(202.85, -72.44) * mm});
            skLineSegment(sketch, "E551", {"start": v(202.85, -72.44) * mm, "end": v(202.85, -69.94) * mm});
            skLineSegment(sketch, "E552", {"start": v(202.85, -69.94) * mm, "end": v(199.75, -69.94) * mm});
            skLineSegment(sketch, "E553", {"start": v(199.75, -69.94) * mm, "end": v(199.75, -72.44) * mm});
            skLineSegment(sketch, "E554", {"start": v(199.75, -72.44) * mm, "end": v(198.5, -72.44) * mm});
            skLineSegment(sketch, "E555", {"start": v(198.5, -72.44) * mm, "end": v(198.5, -74.94) * mm});
            skLineSegment(sketch, "E556", {"start": v(198.5, -74.94) * mm, "end": v(199.75, -74.94) * mm});
            skLineSegment(sketch, "E557", {"start": v(199.75, -74.94) * mm, "end": v(199.75, -77.04) * mm});
            skLineSegment(sketch, "E558", {"start": v(199.75, -77.04) * mm, "end": v(193.3, -77.04) * mm});
            skLineSegment(sketch, "E559", {"start": v(193.3, -77.04) * mm, "end": v(193.3, -80.04) * mm});
            skLineSegment(sketch, "E560", {"start": v(193.3, -80.04) * mm, "end": v(177.3, -80.04) * mm});
            skLineSegment(sketch, "E561", {"start": v(177.3, -80.04) * mm, "end": v(177.3, -77.04) * mm});
            skLineSegment(sketch, "E562", {"start": v(177.3, -77.04) * mm, "end": v(161.3, -77.04) * mm});
            skLineSegment(sketch, "E563", {"start": v(161.3, -77.04) * mm, "end": v(161.3, -64.04) * mm});
            skLineSegment(sketch, "E564", {"start": v(161.3, 15.96) * mm, "end": v(164.3, 15.96) * mm});
            skLineSegment(sketch, "E565", {"start": v(164.3, 15.96) * mm, "end": v(164.3, 31.96) * mm});
            skLineSegment(sketch, "E566", {"start": v(164.3, 31.96) * mm, "end": v(161.3, 31.96) * mm});
            skLineSegment(sketch, "E567", {"start": v(161.3, 31.96) * mm, "end": v(161.3, 38.1) * mm});
            skLineSegment(sketch, "E568", {"start": v(161.3, 38.1) * mm, "end": v(165, 38.1) * mm});
            skLineSegment(sketch, "E569", {"start": v(165, 38.1) * mm, "end": v(165, 41.8) * mm});
            skLineSegment(sketch, "E570", {"start": v(165, 41.8) * mm, "end": v(161.3, 41.8) * mm});
            skLineSegment(sketch, "E571", {"start": v(161.3, 41.8) * mm, "end": v(161.3, 47.96) * mm});
            skLineSegment(sketch, "E572", {"start": v(161.3, 47.96) * mm, "end": v(164.3, 47.96) * mm});
            skLineSegment(sketch, "E573", {"start": v(164.3, 47.96) * mm, "end": v(164.3, 63.96) * mm});
            skLineSegment(sketch, "E574", {"start": v(164.3, 63.96) * mm, "end": v(161.3, 63.96) * mm});
            skLineSegment(sketch, "E575", {"start": v(161.3, 63.96) * mm, "end": v(161.3, 76.96) * mm});
            skLineSegment(sketch, "E576", {"start": v(161.3, 76.96) * mm, "end": v(177.3, 76.96) * mm});
            skLineSegment(sketch, "E577", {"start": v(177.3, 76.96) * mm, "end": v(177.3, 79.96) * mm});
            skLineSegment(sketch, "E578", {"start": v(177.3, 79.96) * mm, "end": v(193.3, 79.96) * mm});
            skLineSegment(sketch, "E579", {"start": v(193.3, 79.96) * mm, "end": v(193.3, 76.96) * mm});
            skLineSegment(sketch, "E580", {"start": v(193.3, 76.96) * mm, "end": v(199.75, 76.96) * mm});
            skLineSegment(sketch, "E581", {"start": v(199.75, 76.96) * mm, "end": v(199.75, 74.86) * mm});
            skLineSegment(sketch, "E582", {"start": v(199.75, 74.86) * mm, "end": v(198.5, 74.86) * mm});
            skLineSegment(sketch, "E583", {"start": v(198.5, 74.86) * mm, "end": v(198.5, 72.36) * mm});
            skLineSegment(sketch, "E584", {"start": v(198.5, 72.36) * mm, "end": v(199.75, 72.36) * mm});
            skLineSegment(sketch, "E585", {"start": v(199.75, 72.36) * mm, "end": v(199.75, 69.86) * mm});
            skLineSegment(sketch, "E586", {"start": v(199.75, 69.86) * mm, "end": v(202.85, 69.86) * mm});
            skLineSegment(sketch, "E587", {"start": v(202.85, 69.86) * mm, "end": v(202.85, 72.36) * mm});
            skLineSegment(sketch, "E588", {"start": v(202.85, 72.36) * mm, "end": v(204.1, 72.36) * mm});
            skLineSegment(sketch, "E589", {"start": v(204.1, 72.36) * mm, "end": v(204.1, 74.86) * mm});
            skLineSegment(sketch, "E590", {"start": v(204.1, 74.86) * mm, "end": v(202.85, 74.86) * mm});
            skLineSegment(sketch, "E591", {"start": v(202.85, 74.86) * mm, "end": v(202.85, 76.96) * mm});
            skLineSegment(sketch, "E592", {"start": v(202.85, 76.96) * mm, "end": v(209.3, 76.96) * mm});
            skLineSegment(sketch, "E593", {"start": v(209.3, 76.96) * mm, "end": v(209.3, 79.96) * mm});
            skLineSegment(sketch, "E594", {"start": v(209.3, 79.96) * mm, "end": v(225.3, 79.96) * mm});
            skLineSegment(sketch, "E595", {"start": v(225.3, 79.96) * mm, "end": v(225.3, 76.96) * mm});
            skLineSegment(sketch, "E596", {"start": v(225.3, 76.96) * mm, "end": v(241.3, 76.96) * mm});
            skLineSegment(sketch, "E597", {"start": v(241.3, 76.96) * mm, "end": v(241.3, 63.96) * mm});
            skLineSegment(sketch, "E598", {"start": v(241.3, 63.96) * mm, "end": v(238.3, 63.96) * mm});
            skLineSegment(sketch, "E599", {"start": v(238.3, 63.96) * mm, "end": v(238.3, 47.96) * mm});
            skLineSegment(sketch, "E600", {"start": v(238.3, 47.96) * mm, "end": v(241.3, 47.96) * mm});
            skLineSegment(sketch, "E601", {"start": v(241.3, 47.96) * mm, "end": v(241.3, 41.8) * mm});
            skLineSegment(sketch, "E602", {"start": v(241.3, 41.8) * mm, "end": v(237.6, 41.8) * mm});
            skLineSegment(sketch, "E603", {"start": v(237.6, 41.8) * mm, "end": v(237.6, 38.1) * mm});
            skLineSegment(sketch, "E604", {"start": v(237.6, 38.1) * mm, "end": v(241.3, 38.1) * mm});
            skLineSegment(sketch, "E605", {"start": v(241.3, 38.1) * mm, "end": v(241.3, 31.96) * mm});
            skLineSegment(sketch, "E606", {"start": v(241.3, 31.96) * mm, "end": v(238.3, 31.96) * mm});
            skLineSegment(sketch, "E607", {"start": v(238.3, 31.96) * mm, "end": v(238.3, 15.96) * mm});
            skLineSegment(sketch, "E608", {"start": v(238.3, 15.96) * mm, "end": v(241.3, 15.96) * mm});
            skLineSegment(sketch, "E609", {"start": v(241.3, 15.96) * mm, "end": v(241.3, 2.96) * mm});
            skLineSegment(sketch, "E610", {"start": v(241.3, 2.96) * mm, "end": v(225.3, 2.96) * mm});
            skLineSegment(sketch, "E611", {"start": v(225.3, 2.96) * mm, "end": v(225.3, -0.04) * mm});
            skLineSegment(sketch, "E612", {"start": v(225.3, -0.04) * mm, "end": v(209.3, -0.04) * mm});
            skLineSegment(sketch, "E613", {"start": v(209.3, -0.04) * mm, "end": v(209.3, 2.96) * mm});
            skLineSegment(sketch, "E614", {"start": v(209.3, 2.96) * mm, "end": v(202.85, 2.96) * mm});
            skLineSegment(sketch, "E615", {"start": v(202.85, 2.96) * mm, "end": v(202.85, 5.06) * mm});
            skLineSegment(sketch, "E616", {"start": v(202.85, 5.06) * mm, "end": v(204.1, 5.06) * mm});
            skLineSegment(sketch, "E617", {"start": v(204.1, 5.06) * mm, "end": v(204.1, 7.56) * mm});
            skLineSegment(sketch, "E618", {"start": v(204.1, 7.56) * mm, "end": v(202.85, 7.56) * mm});
            skLineSegment(sketch, "E619", {"start": v(202.85, 7.56) * mm, "end": v(202.85, 10.06) * mm});
            skLineSegment(sketch, "E620", {"start": v(202.85, 10.06) * mm, "end": v(199.75, 10.06) * mm});
            skLineSegment(sketch, "E621", {"start": v(199.75, 10.06) * mm, "end": v(199.75, 7.56) * mm});
            skLineSegment(sketch, "E622", {"start": v(199.75, 7.56) * mm, "end": v(198.5, 7.56) * mm});
            skLineSegment(sketch, "E623", {"start": v(198.5, 7.56) * mm, "end": v(198.5, 5.06) * mm});
            skLineSegment(sketch, "E624", {"start": v(198.5, 5.06) * mm, "end": v(199.75, 5.06) * mm});
            skLineSegment(sketch, "E625", {"start": v(199.75, 5.06) * mm, "end": v(199.75, 2.96) * mm});
            skLineSegment(sketch, "E626", {"start": v(199.75, 2.96) * mm, "end": v(193.3, 2.96) * mm});
            skLineSegment(sketch, "E627", {"start": v(193.3, 2.96) * mm, "end": v(193.3, -0.04) * mm});
            skLineSegment(sketch, "E628", {"start": v(193.3, -0.04) * mm, "end": v(177.3, -0.04) * mm});
            skLineSegment(sketch, "E629", {"start": v(177.3, -0.04) * mm, "end": v(177.3, 2.96) * mm});
            skLineSegment(sketch, "E630", {"start": v(177.3, 2.96) * mm, "end": v(161.3, 2.96) * mm});
            skLineSegment(sketch, "E631", {"start": v(161.3, 2.96) * mm, "end": v(161.3, 15.96) * mm});
            skLineSegment(sketch, "E632", {"start": v(-238.7, 2.96) * mm, "end": v(-238.7, 15.96) * mm});
            skLineSegment(sketch, "E633", {"start": v(-238.7, 31.96) * mm, "end": v(-238.7, 38.1) * mm});
            skLineSegment(sketch, "E634", {"start": v(-238.7, 41.8) * mm, "end": v(-238.7, 47.96) * mm});
            skLineSegment(sketch, "E635", {"start": v(-238.7, 63.96) * mm, "end": v(-238.7, 76.96) * mm});
            skLineSegment(sketch, "E636", {"start": v(-220.2, 79.96) * mm, "end": v(-212.8, 79.96) * mm});
            skLineSegment(sketch, "E637", {"start": v(-212.8, 79.96) * mm, "end": v(-212.8, 76.26) * mm});
            skLineSegment(sketch, "E638", {"start": v(-212.8, 76.26) * mm, "end": v(-209.1, 76.26) * mm});
            skLineSegment(sketch, "E639", {"start": v(-209.1, 76.26) * mm, "end": v(-209.1, 79.96) * mm});
            skLineSegment(sketch, "E640", {"start": v(-209.1, 79.96) * mm, "end": v(-201.7, 79.96) * mm});
            skLineSegment(sketch, "E641", {"start": v(-187.7, 79.96) * mm, "end": v(-173.7, 79.96) * mm});
            skLineSegment(sketch, "E642", {"start": v(-159.7, 79.96) * mm, "end": v(-145.7, 79.96) * mm});
            skLineSegment(sketch, "E643", {"start": v(-131.7, 79.96) * mm, "end": v(-117.7, 79.96) * mm});
            skLineSegment(sketch, "E644", {"start": v(-103.7, 79.96) * mm, "end": v(-89.7, 79.96) * mm});
            skLineSegment(sketch, "E645", {"start": v(-75.7, 79.96) * mm, "end": v(-68.3, 79.96) * mm});
            skLineSegment(sketch, "E646", {"start": v(-68.3, 79.96) * mm, "end": v(-68.3, 76.26) * mm});
            skLineSegment(sketch, "E647", {"start": v(-68.3, 76.26) * mm, "end": v(-64.6, 76.26) * mm});
            skLineSegment(sketch, "E648", {"start": v(-64.6, 76.26) * mm, "end": v(-64.6, 79.96) * mm});
            skLineSegment(sketch, "E649", {"start": v(-64.6, 79.96) * mm, "end": v(-57.2, 79.96) * mm});
            skLineSegment(sketch, "E650", {"start": v(-38.7, 76.96) * mm, "end": v(-38.7, 63.96) * mm});
            skLineSegment(sketch, "E651", {"start": v(-38.7, 47.96) * mm, "end": v(-38.7, 41.8) * mm});
            skLineSegment(sketch, "E652", {"start": v(-38.7, 38.1) * mm, "end": v(-38.7, 31.96) * mm});
            skLineSegment(sketch, "E653", {"start": v(-38.7, 15.96) * mm, "end": v(-38.7, 2.96) * mm});
            skLineSegment(sketch, "E654", {"start": v(-57.2, -0.04) * mm, "end": v(-64.6, -0.04) * mm});
            skLineSegment(sketch, "E655", {"start": v(-64.6, -0.04) * mm, "end": v(-64.6, 3.66) * mm});
            skLineSegment(sketch, "E656", {"start": v(-64.6, 3.66) * mm, "end": v(-68.3, 3.66) * mm});
            skLineSegment(sketch, "E657", {"start": v(-68.3, 3.66) * mm, "end": v(-68.3, -0.04) * mm});
            skLineSegment(sketch, "E658", {"start": v(-68.3, -0.04) * mm, "end": v(-75.7, -0.04) * mm});
            skLineSegment(sketch, "E659", {"start": v(-89.7, -0.04) * mm, "end": v(-103.7, -0.04) * mm});
            skLineSegment(sketch, "E660", {"start": v(-117.7, -0.04) * mm, "end": v(-131.7, -0.04) * mm});
            skLineSegment(sketch, "E661", {"start": v(-145.7, -0.04) * mm, "end": v(-159.7, -0.04) * mm});
            skLineSegment(sketch, "E662", {"start": v(-173.7, -0.04) * mm, "end": v(-187.7, -0.04) * mm});
            skLineSegment(sketch, "E663", {"start": v(-201.7, -0.04) * mm, "end": v(-209.1, -0.04) * mm});
            skLineSegment(sketch, "E664", {"start": v(-209.1, -0.04) * mm, "end": v(-209.1, 3.66) * mm});
            skLineSegment(sketch, "E665", {"start": v(-209.1, 3.66) * mm, "end": v(-212.8, 3.66) * mm});
            skLineSegment(sketch, "E666", {"start": v(-212.8, 3.66) * mm, "end": v(-212.8, -0.04) * mm});
            skLineSegment(sketch, "E667", {"start": v(-212.8, -0.04) * mm, "end": v(-220.2, -0.04) * mm});
            skLineSegment(sketch, "E668", {"start": v(-38.7, 15.96) * mm, "end": v(-35.7, 15.96) * mm});
            skLineSegment(sketch, "E669", {"start": v(-35.7, 15.96) * mm, "end": v(-35.7, 31.96) * mm});
            skLineSegment(sketch, "E670", {"start": v(-35.7, 31.96) * mm, "end": v(-38.7, 31.96) * mm});
            skLineSegment(sketch, "E671", {"start": v(-38.7, 31.96) * mm, "end": v(-38.7, 38.1) * mm});
            skLineSegment(sketch, "E672", {"start": v(-38.7, 38.1) * mm, "end": v(-35, 38.1) * mm});
            skLineSegment(sketch, "E673", {"start": v(-35, 38.1) * mm, "end": v(-35, 41.8) * mm});
            skLineSegment(sketch, "E674", {"start": v(-35, 41.8) * mm, "end": v(-38.7, 41.8) * mm});
            skLineSegment(sketch, "E675", {"start": v(-38.7, 41.8) * mm, "end": v(-38.7, 47.96) * mm});
            skLineSegment(sketch, "E676", {"start": v(-38.7, 47.96) * mm, "end": v(-35.7, 47.96) * mm});
            skLineSegment(sketch, "E677", {"start": v(-35.7, 47.96) * mm, "end": v(-35.7, 63.96) * mm});
            skLineSegment(sketch, "E678", {"start": v(-35.7, 63.96) * mm, "end": v(-38.7, 63.96) * mm});
            skLineSegment(sketch, "E679", {"start": v(-38.7, 63.96) * mm, "end": v(-38.7, 76.96) * mm});
            skLineSegment(sketch, "E680", {"start": v(-38.7, 76.96) * mm, "end": v(-20.2, 76.96) * mm});
            skLineSegment(sketch, "E681", {"start": v(-20.2, 76.96) * mm, "end": v(-20.2, 79.96) * mm});
            skLineSegment(sketch, "E682", {"start": v(-20.2, 79.96) * mm, "end": v(-12.8, 79.96) * mm});
            skLineSegment(sketch, "E683", {"start": v(-12.8, 79.96) * mm, "end": v(-12.8, 76.26) * mm});
            skLineSegment(sketch, "E684", {"start": v(-12.8, 76.26) * mm, "end": v(-9.1, 76.26) * mm});
            skLineSegment(sketch, "E685", {"start": v(-9.1, 76.26) * mm, "end": v(-9.1, 79.96) * mm});
            skLineSegment(sketch, "E686", {"start": v(-9.1, 79.96) * mm, "end": v(-1.7, 79.96) * mm});
            skLineSegment(sketch, "E687", {"start": v(-1.7, 79.96) * mm, "end": v(-1.7, 76.96) * mm});
            skLineSegment(sketch, "E688", {"start": v(-1.7, 76.96) * mm, "end": v(12.3, 76.96) * mm});
            skLineSegment(sketch, "E689", {"start": v(12.3, 76.96) * mm, "end": v(12.3, 79.96) * mm});
            skLineSegment(sketch, "E690", {"start": v(12.3, 79.96) * mm, "end": v(26.3, 79.96) * mm});
            skLineSegment(sketch, "E691", {"start": v(26.3, 79.96) * mm, "end": v(26.3, 76.96) * mm});
            skLineSegment(sketch, "E692", {"start": v(26.3, 76.96) * mm, "end": v(40.3, 76.96) * mm});
            skLineSegment(sketch, "E693", {"start": v(40.3, 76.96) * mm, "end": v(40.3, 79.96) * mm});
            skLineSegment(sketch, "E694", {"start": v(40.3, 79.96) * mm, "end": v(54.3, 79.96) * mm});
            skLineSegment(sketch, "E695", {"start": v(54.3, 79.96) * mm, "end": v(54.3, 76.96) * mm});
            skLineSegment(sketch, "E696", {"start": v(54.3, 76.96) * mm, "end": v(68.3, 76.96) * mm});
            skLineSegment(sketch, "E697", {"start": v(68.3, 76.96) * mm, "end": v(68.3, 79.96) * mm});
            skLineSegment(sketch, "E698", {"start": v(68.3, 79.96) * mm, "end": v(82.3, 79.96) * mm});
            skLineSegment(sketch, "E699", {"start": v(82.3, 79.96) * mm, "end": v(82.3, 76.96) * mm});
            skLineSegment(sketch, "E700", {"start": v(82.3, 76.96) * mm, "end": v(96.3, 76.96) * mm});
            skLineSegment(sketch, "E701", {"start": v(96.3, 76.96) * mm, "end": v(96.3, 79.96) * mm});
            skLineSegment(sketch, "E702", {"start": v(96.3, 79.96) * mm, "end": v(110.3, 79.96) * mm});
            skLineSegment(sketch, "E703", {"start": v(110.3, 79.96) * mm, "end": v(110.3, 76.96) * mm});
            skLineSegment(sketch, "E704", {"start": v(110.3, 76.96) * mm, "end": v(124.3, 76.96) * mm});
            skLineSegment(sketch, "E705", {"start": v(124.3, 76.96) * mm, "end": v(124.3, 79.96) * mm});
            skLineSegment(sketch, "E706", {"start": v(124.3, 79.96) * mm, "end": v(131.7, 79.96) * mm});
            skLineSegment(sketch, "E707", {"start": v(131.7, 79.96) * mm, "end": v(131.7, 76.26) * mm});
            skLineSegment(sketch, "E708", {"start": v(131.7, 76.26) * mm, "end": v(135.4, 76.26) * mm});
            skLineSegment(sketch, "E709", {"start": v(135.4, 76.26) * mm, "end": v(135.4, 79.96) * mm});
            skLineSegment(sketch, "E710", {"start": v(135.4, 79.96) * mm, "end": v(142.8, 79.96) * mm});
            skLineSegment(sketch, "E711", {"start": v(142.8, 79.96) * mm, "end": v(142.8, 76.96) * mm});
            skLineSegment(sketch, "E712", {"start": v(142.8, 76.96) * mm, "end": v(161.3, 76.96) * mm});
            skLineSegment(sketch, "E713", {"start": v(161.3, 76.96) * mm, "end": v(161.3, 63.96) * mm});
            skLineSegment(sketch, "E714", {"start": v(161.3, 63.96) * mm, "end": v(158.3, 63.96) * mm});
            skLineSegment(sketch, "E715", {"start": v(158.3, 63.96) * mm, "end": v(158.3, 47.96) * mm});
            skLineSegment(sketch, "E716", {"start": v(158.3, 47.96) * mm, "end": v(161.3, 47.96) * mm});
            skLineSegment(sketch, "E717", {"start": v(161.3, 47.96) * mm, "end": v(161.3, 41.8) * mm});
            skLineSegment(sketch, "E718", {"start": v(161.3, 41.8) * mm, "end": v(157.6, 41.8) * mm});
            skLineSegment(sketch, "E719", {"start": v(157.6, 41.8) * mm, "end": v(157.6, 38.1) * mm});
            skLineSegment(sketch, "E720", {"start": v(157.6, 38.1) * mm, "end": v(161.3, 38.1) * mm});
            skLineSegment(sketch, "E721", {"start": v(161.3, 38.1) * mm, "end": v(161.3, 31.96) * mm});
            skLineSegment(sketch, "E722", {"start": v(161.3, 31.96) * mm, "end": v(158.3, 31.96) * mm});
            skLineSegment(sketch, "E723", {"start": v(158.3, 31.96) * mm, "end": v(158.3, 15.96) * mm});
            skLineSegment(sketch, "E724", {"start": v(158.3, 15.96) * mm, "end": v(161.3, 15.96) * mm});
            skLineSegment(sketch, "E725", {"start": v(161.3, 15.96) * mm, "end": v(161.3, 2.96) * mm});
            skLineSegment(sketch, "E726", {"start": v(161.3, 2.96) * mm, "end": v(142.8, 2.96) * mm});
            skLineSegment(sketch, "E727", {"start": v(142.8, 2.96) * mm, "end": v(142.8, -0.04) * mm});
            skLineSegment(sketch, "E728", {"start": v(142.8, -0.04) * mm, "end": v(135.4, -0.04) * mm});
            skLineSegment(sketch, "E729", {"start": v(135.4, -0.04) * mm, "end": v(135.4, 3.66) * mm});
            skLineSegment(sketch, "E730", {"start": v(135.4, 3.66) * mm, "end": v(131.7, 3.66) * mm});
            skLineSegment(sketch, "E731", {"start": v(131.7, 3.66) * mm, "end": v(131.7, -0.04) * mm});
            skLineSegment(sketch, "E732", {"start": v(131.7, -0.04) * mm, "end": v(124.3, -0.04) * mm});
            skLineSegment(sketch, "E733", {"start": v(124.3, -0.04) * mm, "end": v(124.3, 2.96) * mm});
            skLineSegment(sketch, "E734", {"start": v(124.3, 2.96) * mm, "end": v(110.3, 2.96) * mm});
            skLineSegment(sketch, "E735", {"start": v(110.3, 2.96) * mm, "end": v(110.3, -0.04) * mm});
            skLineSegment(sketch, "E736", {"start": v(110.3, -0.04) * mm, "end": v(96.3, -0.04) * mm});
            skLineSegment(sketch, "E737", {"start": v(96.3, -0.04) * mm, "end": v(96.3, 2.96) * mm});
            skLineSegment(sketch, "E738", {"start": v(96.3, 2.96) * mm, "end": v(82.3, 2.96) * mm});
            skLineSegment(sketch, "E739", {"start": v(82.3, 2.96) * mm, "end": v(82.3, -0.04) * mm});
            skLineSegment(sketch, "E740", {"start": v(82.3, -0.04) * mm, "end": v(68.3, -0.04) * mm});
            skLineSegment(sketch, "E741", {"start": v(68.3, -0.04) * mm, "end": v(68.3, 2.96) * mm});
            skLineSegment(sketch, "E742", {"start": v(68.3, 2.96) * mm, "end": v(54.3, 2.96) * mm});
            skLineSegment(sketch, "E743", {"start": v(54.3, 2.96) * mm, "end": v(54.3, -0.04) * mm});
            skLineSegment(sketch, "E744", {"start": v(54.3, -0.04) * mm, "end": v(40.3, -0.04) * mm});
            skLineSegment(sketch, "E745", {"start": v(40.3, -0.04) * mm, "end": v(40.3, 2.96) * mm});
            skLineSegment(sketch, "E746", {"start": v(40.3, 2.96) * mm, "end": v(26.3, 2.96) * mm});
            skLineSegment(sketch, "E747", {"start": v(26.3, 2.96) * mm, "end": v(26.3, -0.04) * mm});
            skLineSegment(sketch, "E748", {"start": v(26.3, -0.04) * mm, "end": v(12.3, -0.04) * mm});
            skLineSegment(sketch, "E749", {"start": v(12.3, -0.04) * mm, "end": v(12.3, 2.96) * mm});
            skLineSegment(sketch, "E750", {"start": v(12.3, 2.96) * mm, "end": v(-1.7, 2.96) * mm});
            skLineSegment(sketch, "E751", {"start": v(-1.7, 2.96) * mm, "end": v(-1.7, -0.04) * mm});
            skLineSegment(sketch, "E752", {"start": v(-1.7, -0.04) * mm, "end": v(-9.1, -0.04) * mm});
            skLineSegment(sketch, "E753", {"start": v(-9.1, -0.04) * mm, "end": v(-9.1, 3.66) * mm});
            skLineSegment(sketch, "E754", {"start": v(-9.1, 3.66) * mm, "end": v(-12.8, 3.66) * mm});
            skLineSegment(sketch, "E755", {"start": v(-12.8, 3.66) * mm, "end": v(-12.8, -0.04) * mm});
            skLineSegment(sketch, "E756", {"start": v(-12.8, -0.04) * mm, "end": v(-20.2, -0.04) * mm});
            skLineSegment(sketch, "E757", {"start": v(-20.2, -0.04) * mm, "end": v(-20.2, 2.96) * mm});
            skLineSegment(sketch, "E758", {"start": v(-20.2, 2.96) * mm, "end": v(-38.7, 2.96) * mm});
            skLineSegment(sketch, "E759", {"start": v(-38.7, 2.96) * mm, "end": v(-38.7, 15.96) * mm});
            skLineSegment(sketch, "E760", {"start": v(-38.7, 79.96) * mm, "end": v(-238.7, 79.96) * mm});
            skLineSegment(sketch, "E761", {"start": v(-238.7, 79.96) * mm, "end": v(-238.7, -0.04) * mm});
            skLineSegment(sketch, "E762", {"start": v(-238.7, -0.04) * mm, "end": v(-38.7, -0.04) * mm});
            skLineSegment(sketch, "E763", {"start": v(-38.7, -0.04) * mm, "end": v(-38.7, 79.96) * mm});
            skLineSegment(sketch, "E764", {"start": v(-9.4, -77.04) * mm, "end": v(-12.5, -77.04) * mm});
            skLineSegment(sketch, "E765", {"start": v(-64.9, -77.04) * mm, "end": v(-68, -77.04) * mm});
            skLineSegment(sketch, "E766", {"start": v(132, -77.04) * mm, "end": v(135.1, -77.04) * mm});
            skLineSegment(sketch, "E767", {"start": v(-212.5, -77.04) * mm, "end": v(-209.4, -77.04) * mm});
            skSolve(sketch);
        }
        {
            var Q0;
            Q0=makeQuery(id+"F3.imprint","IMPRINT",FACE,{"disambiguationData":[TD([[makeQuery(id+"F3.imprint","IMPRINT",EDGE,{"derivedFrom":sQuery(id+"F3.wireOp",EDGE,"E341")}),1.0]])]});
            var Q1;
            Q1=makeQuery(id+"F3.imprint","IMPRINT",FACE,{"disambiguationData":[TD([[makeQuery(id+"F3.imprint","IMPRINT",EDGE,{"derivedFrom":sQuery(id+"F3.wireOp",EDGE,"E309")}),1.0]])]});
            extrude(context, id + "F4", {"entities" : qUnion([Q0, Q1]), "operationType" : NewBodyOperationType.REMOVE, "oppositeDirection" : true, "depth" : 25 * mm});
        }
        {
            var Q0;
            Q0=makeQuery(id+"F3.imprint","IMPRINT",FACE,{"disambiguationData":[TD([[makeQuery(id+"F3.imprint","IMPRINT",EDGE,{"derivedFrom":sQuery(id+"F3.wireOp",EDGE,"E481")}),1.0]])]});
            var Q1;
            Q1=makeQuery(id+"F3.imprint","IMPRINT",FACE,{"disambiguationData":[TD([[makeQuery(id+"F3.imprint","IMPRINT",EDGE,{"derivedFrom":sQuery(id+"F3.wireOp",EDGE,"E449")}),1.0]])]});
            extrude(context, id + "F5", {"entities" : qUnion([Q0, Q1]), "operationType" : NewBodyOperationType.REMOVE, "oppositeDirection" : true, "depth" : 25 * mm});
        }
        {
            var Q0;
            {var subQ14=sQuery(id+"F3.wireOp",EDGE,"E637");Q0=makeQuery(id+"F3.imprint","IMPRINT",FACE,{"disambiguationData":[TD([[makeQuery(id+"F3.imprint","IMPRINT",EDGE,{"derivedFrom":subQ14}),-1.0]])]});}
            extrude(context, id + "F6", {"entities" : qUnion([Q0]), "operationType" : NewBodyOperationType.ADD, "depth" : 10 * mm});
        }
        {
            var Q0;
            {var subQ0=sQuery(id+"F3.wireOp",EDGE,"E637");Q0=makeQuery(id+"F3.imprint","IMPRINT",FACE,{"disambiguationData":[TD([[makeQuery(id+"F3.imprint","IMPRINT",EDGE,{"derivedFrom":subQ0}),1.0]])]});}
            var Q1;
            {var subQ0=sQuery(id+"F3.wireOp",EDGE,"E664");Q1=makeQuery(id+"F3.imprint","IMPRINT",FACE,{"disambiguationData":[TD([[makeQuery(id+"F3.imprint","IMPRINT",EDGE,{"derivedFrom":subQ0}),1.0]])]});}
            var Q2;
            {var subQ0=sQuery(id+"F3.wireOp",EDGE,"E646");Q2=makeQuery(id+"F3.imprint","IMPRINT",FACE,{"disambiguationData":[TD([[makeQuery(id+"F3.imprint","IMPRINT",EDGE,{"derivedFrom":subQ0}),1.0]])]});}
            var Q3;
            {var subQ0=sQuery(id+"F3.wireOp",EDGE,"E655");Q3=makeQuery(id+"F3.imprint","IMPRINT",FACE,{"disambiguationData":[TD([[makeQuery(id+"F3.imprint","IMPRINT",EDGE,{"derivedFrom":subQ0}),1.0]])]});}
            extrude(context, id + "F7", {"entities" : qUnion([Q0, Q1, Q2, Q3]), "operationType" : NewBodyOperationType.REMOVE, "oppositeDirection" : true, "depth" : 25 * mm});
        }
        {
            var Q0;
            Q0=makeQuery(id+"F3.imprint","IMPRINT",FACE,{"disambiguationData":[TD([[makeQuery(id+"F3.imprint","IMPRINT",EDGE,{"derivedFrom":sQuery(id+"F3.wireOp",EDGE,"E309")}),1.0]])]});
            var Q1;
            Q1=makeQuery(id+"F3.imprint","IMPRINT",FACE,{"disambiguationData":[TD([[makeQuery(id+"F3.imprint","IMPRINT",EDGE,{"derivedFrom":sQuery(id+"F3.wireOp",EDGE,"E341")}),1.0]])]});
            var Q2;
            Q2=makeQuery(id+"F3.imprint","IMPRINT",FACE,{"disambiguationData":[TD([[makeQuery(id+"F3.imprint","IMPRINT",EDGE,{"derivedFrom":sQuery(id+"F3.wireOp",EDGE,"E481")}),1.0]])]});
            var Q3;
            Q3=makeQuery(id+"F3.imprint","IMPRINT",FACE,{"disambiguationData":[TD([[makeQuery(id+"F3.imprint","IMPRINT",EDGE,{"derivedFrom":sQuery(id+"F3.wireOp",EDGE,"E449")}),1.0]])]});
            extrude(context, id + "F8", {"entities" : qUnion([Q0, Q1, Q2, Q3]), "operationType" : NewBodyOperationType.REMOVE, "oppositeDirection" : true, "depth" : 25 * mm});
        }
    });
